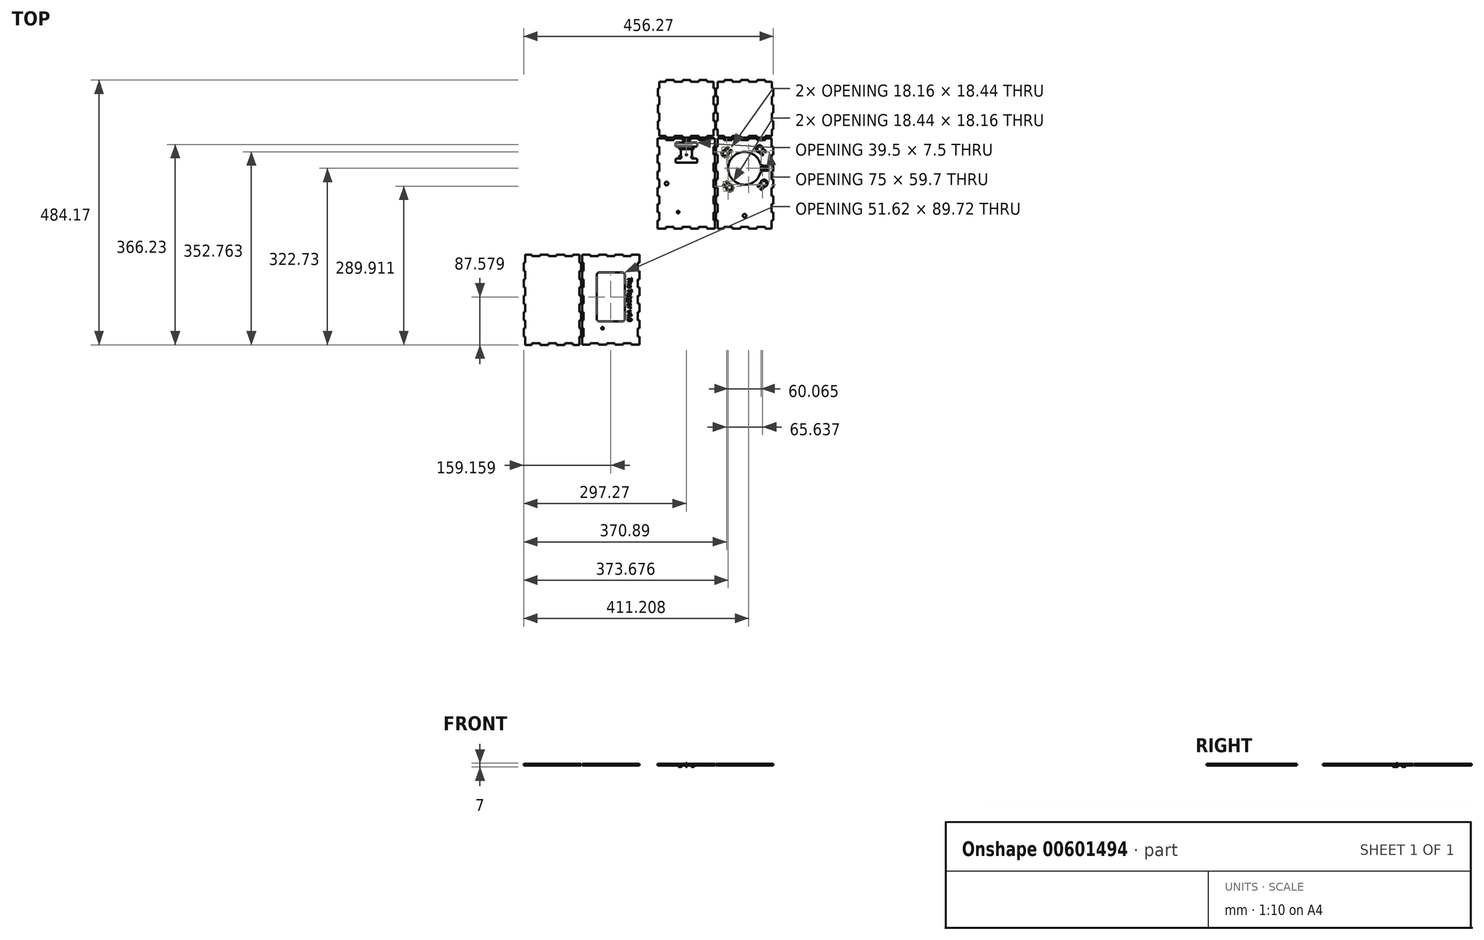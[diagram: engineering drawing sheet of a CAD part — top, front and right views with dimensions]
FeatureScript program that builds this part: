
annotation { "Feature Type Name" : "Feature", "Feature Type Description" : "" }
export const myFeature = defineFeature(function(context is Context, id is Id, definition is map)
    precondition{}
    {
        {
            assignVariable(context, id + "F0", {"name" : "holeNeckDepth", "anyValue" : 3});
        }
        {
            assignVariable(context, id + "F1", {"name" : "woodTh", "anyValue" : 3});
        }
        {
            var Q0;
            Q0=qCreatedBy(makeId("Top.planeOp"),FACE);
            var sketch = newSketch(context, id + "F2", { "sketchPlane" : qUnion([Q0])});
            skLineSegment(sketch, "E0", {"start": v(0, 0) * mm, "end": v(11.88, 0) * mm, "construction": true});
            skLineSegment(sketch, "E1", {"start": v(11.88, 0) * mm, "end": v(11.88, 8.12) * mm, "construction": true});
            skCircle(sketch, "E2", {"center": v(11.88, 8.12) * mm, "radius": 2.88 * mm});
            skCircle(sketch, "E3", {"center": v(11.88, 8.12) * mm, "radius": 1.5 * mm});
            skLineSegment(sketch, "E4", {"start": v(0, 8.12) * mm, "end": v(0, 0) * mm, "construction": true});
            skCircle(sketch, "E5.MirrorC", {"center": v(11.88, -8.12) * mm, "radius": 1.5 * mm});
            skCircle(sketch, "E6.MirrorC", {"center": v(11.88, -8.12) * mm, "radius": 2.88 * mm});
            skCircle(sketch, "E7.MirrorC", {"center": v(-11.88, -8.12) * mm, "radius": 2.88 * mm});
            skCircle(sketch, "E8.MirrorC", {"center": v(-11.88, 8.12) * mm, "radius": 2.88 * mm});
            skCircle(sketch, "E9.MirrorC", {"center": v(-11.88, 8.12) * mm, "radius": 1.5 * mm});
            skCircle(sketch, "E10.MirrorC", {"center": v(-11.88, -8.12) * mm, "radius": 1.5 * mm});
            skLineSegment(sketch, "E11", {"start": v(11.88, -5.25) * mm, "end": v(-11.88, -5.25) * mm, "construction": true});
            skLineSegment(sketch, "E12", {"start": v(0, -5.25) * mm, "end": v(0, -3.75) * mm, "construction": true});
            skPoint(sketch, "E12.endSnap0", {"position": v(0, -5.25) * mm});
            skCircle(sketch, "E13", {"center": v(0, -3.75) * mm, "radius": 1.3 * mm});
            skSolve(sketch);
        }
        {
            var Q0;
            Q0=makeQuery(id+"F2.imprint","IMPRINT",FACE,{"disambiguationData":[TD([[makeQuery(id+"F2.imprint","IMPRINT",EDGE,{"derivedFrom":sQuery(id+"F2.wireOp",EDGE,"E8.MirrorC")}),-1.0]])]});
            var Q1;
            Q1=makeQuery(id+"F2.imprint","IMPRINT",FACE,{"disambiguationData":[TD([[makeQuery(id+"F2.imprint","IMPRINT",EDGE,{"derivedFrom":sQuery(id+"F2.wireOp",EDGE,"E2")}),1.0]])]});
            var Q2;
            Q2=makeQuery(id+"F2.imprint","IMPRINT",FACE,{"disambiguationData":[TD([[makeQuery(id+"F2.imprint","IMPRINT",EDGE,{"derivedFrom":sQuery(id+"F2.wireOp",EDGE,"E5.MirrorC")}),1.0]])]});
            var Q3;
            Q3=makeQuery(id+"F2.imprint","IMPRINT",FACE,{"disambiguationData":[TD([[makeQuery(id+"F2.imprint","IMPRINT",EDGE,{"derivedFrom":sQuery(id+"F2.wireOp",EDGE,"E7.MirrorC")}),1.0]])]});
            extrude(context, id + "F3", {"entities" : qUnion([Q0, Q1, Q2, Q3]), "depth" : (getVariable(context, 'holeNeckDepth') * 2) * mm, "offsetDistance" : 25 * mm});
        }
        {
            var Q0;
            Q0=qCreatedBy(makeId("Top.planeOp"),FACE);
            cPlane(context, id + "F4", {"entities" : qUnion([Q0]), "cplaneType" : CPlaneType.OFFSET, "offset" : (getVariable(context, 'holeNeckDepth') * 2) * mm, "width" : 150 * mm, "height" : 150 * mm});
        }
        {
            var Q0;
            Q0=qCreatedBy(id+"F4.planeOp",FACE);
            var sketch = newSketch(context, id + "F5", { "sketchPlane" : qUnion([Q0])});
            skLineSegment(sketch, "E14", {"start": v(9.42, 6.63) * mm, "end": v(-9.42, 6.63) * mm});
            skLineSegment(sketch, "E15", {"start": v(-11.88, 11) * mm, "end": v(11.88, 11) * mm});
            skLineSegment(sketch, "E16", {"start": v(14.75, 8.12) * mm, "end": v(14.75, -8.12) * mm, "construction": true});
            skLineSegment(sketch, "E17", {"start": v(10.38, 5.67) * mm, "end": v(10.38, -5.67) * mm});
            skLineSegment(sketch, "E18", {"start": v(-10.38, 5.67) * mm, "end": v(-10.38, -5.67) * mm});
            skLineSegment(sketch, "E19", {"start": v(-14.75, 8.12) * mm, "end": v(-14.75, -8.12) * mm, "construction": true});
            skLineSegment(sketch, "E20", {"start": v(11.88, 11) * mm, "end": v(52.5, 11) * mm, "construction": true});
            skArc(sketch, "E21.0", {"start": v(-9.42, 6.63) * mm, "mid": v(-9.84, 6.1) * mm, "end": v(-10.38, 5.67) * mm});
            skArc(sketch, "E22.0", {"start": v(-11.88, -11) * mm, "mid": v(-9.1, -8.9) * mm, "end": v(-10.38, -5.67) * mm});
            skArc(sketch, "E23.0", {"start": v(11.88, -11) * mm, "mid": v(9.1, -8.9) * mm, "end": v(10.38, -5.67) * mm});
            skArc(sketch, "E24.0", {"start": v(9.42, 6.63) * mm, "mid": v(9.84, 6.1) * mm, "end": v(10.38, 5.67) * mm});
            skLineSegment(sketch, "E25.MirrorCS", {"start": v(11.88, -11) * mm, "end": v(52.5, -11) * mm, "construction": true});
            skLineSegment(sketch, "E26.MirrorCS", {"start": v(-11.88, -11) * mm, "end": v(-52.5, -11) * mm, "construction": true});
            skLineSegment(sketch, "E27.MirrorCS", {"start": v(-11.88, 11) * mm, "end": v(-52.5, 11) * mm, "construction": true});
            skCircle(sketch, "E28.0", {"center": v(-11.88, 8.12) * mm, "radius": 1.5 * mm});
            skCircle(sketch, "E29.0", {"center": v(11.88, -8.12) * mm, "radius": 1.5 * mm});
            skCircle(sketch, "E30.0", {"center": v(-11.88, -8.12) * mm, "radius": 1.5 * mm});
            skLineSegment(sketch, "E31", {"start": v(52.5, 26) * mm, "end": v(52.5, 11) * mm});
            skLineSegment(sketch, "E32", {"start": v(52.5, 11) * mm, "end": v(49.5, 11) * mm});
            skLineSegment(sketch, "E33", {"start": v(32.19, 11) * mm, "end": v(32.19, 26) * mm, "construction": true});
            skLineSegment(sketch, "E34", {"start": v(49.5, 11) * mm, "end": v(49.5, -4) * mm});
            skLineSegment(sketch, "E35", {"start": v(49.5, -4) * mm, "end": v(52.5, -4) * mm});
            skLineSegment(sketch, "E36", {"start": v(14.75, 8.12) * mm, "end": v(14.75, 11) * mm, "construction": true});
            skLineSegment(sketch, "E37", {"start": v(14.75, 11) * mm, "end": v(17.75, 11) * mm});
            skLineSegment(sketch, "E38", {"start": v(19.75, 13) * mm, "end": v(19.75, 16.5) * mm});
            skLineSegment(sketch, "E39", {"start": v(17.75, 18.5) * mm, "end": v(0, 18.5) * mm});
            skPoint(sketch, "E39.endSnap0", {"position": v(0, 6.63) * mm});
            skLineSegment(sketch, "E40.MirrorCS", {"start": v(-14.75, 11) * mm, "end": v(-17.75, 11) * mm});
            skLineSegment(sketch, "E41.MirrorCS", {"start": v(-14.75, 8.12) * mm, "end": v(-14.75, 11) * mm, "construction": true});
            skLineSegment(sketch, "E42.MirrorCS", {"start": v(-17.75, 18.5) * mm, "end": v(0, 18.5) * mm});
            skLineSegment(sketch, "E43.MirrorCS", {"start": v(-19.75, 13) * mm, "end": v(-19.75, 16.5) * mm});
            skLineSegment(sketch, "E44.MirrorCS", {"start": v(-14.75, -8.12) * mm, "end": v(-14.75, -11) * mm, "construction": true});
            skLineSegment(sketch, "E45.MirrorCS", {"start": v(14.75, -8.12) * mm, "end": v(14.75, -11) * mm, "construction": true});
            skLineSegment(sketch, "E46.MirrorCS", {"start": v(19.75, -13) * mm, "end": v(19.75, -16.5) * mm});
            skLineSegment(sketch, "E47.MirrorCS", {"start": v(14.75, -11) * mm, "end": v(17.75, -11) * mm});
            skLineSegment(sketch, "E48.MirrorCS", {"start": v(17.75, -18.5) * mm, "end": v(0, -18.5) * mm});
            skLineSegment(sketch, "E49.MirrorCS", {"start": v(-14.75, -11) * mm, "end": v(-17.75, -11) * mm});
            skLineSegment(sketch, "E50.MirrorCS", {"start": v(-19.75, -13) * mm, "end": v(-19.75, -16.5) * mm});
            skLineSegment(sketch, "E51.MirrorCS", {"start": v(-17.75, -18.5) * mm, "end": v(0, -18.5) * mm});
            skLineSegment(sketch, "E52", {"start": v(52.5, 26) * mm, "end": v(45.43, 18.93) * mm, "construction": true});
            skLineSegment(sketch, "E53.MirrorCS", {"start": v(37.5, 26) * mm, "end": v(37.5, 23) * mm});
            skLineSegment(sketch, "E54.MirrorCS", {"start": v(37.5, 23) * mm, "end": v(22.5, 23) * mm});
            skLineSegment(sketch, "E55.MirrorCS", {"start": v(22.5, 23) * mm, "end": v(22.5, 26) * mm});
            skLineSegment(sketch, "E56.MirrorCS", {"start": v(52.5, 26) * mm, "end": v(37.5, 26) * mm});
            skLineSegment(sketch, "E57.1.0.0", {"start": v(7.5, 23) * mm, "end": v(-7.5, 23) * mm});
            skLineSegment(sketch, "E57.1.0.1", {"start": v(-7.5, 23) * mm, "end": v(-7.5, 26) * mm});
            skLineSegment(sketch, "E57.1.0.2", {"start": v(7.5, 26) * mm, "end": v(7.5, 23) * mm});
            skLineSegment(sketch, "E57.1.0.3", {"start": v(22.5, 26) * mm, "end": v(7.5, 26) * mm});
            skLineSegment(sketch, "E57.2.0.0", {"start": v(-22.5, 23) * mm, "end": v(-37.5, 23) * mm});
            skLineSegment(sketch, "E57.2.0.1", {"start": v(-37.5, 23) * mm, "end": v(-37.5, 26) * mm});
            skLineSegment(sketch, "E57.2.0.2", {"start": v(-22.5, 26) * mm, "end": v(-22.5, 23) * mm});
            skLineSegment(sketch, "E57.2.0.3", {"start": v(-7.5, 26) * mm, "end": v(-22.5, 26) * mm});
            skLineSegment(sketch, "E57.direction1", {"start": v(22.5, 23) * mm, "end": v(-7.5, 23) * mm, "construction": true});
            skLineSegment(sketch, "E58", {"start": v(-37.5, 26) * mm, "end": v(-52.5, 26) * mm});
            skLineSegment(sketch, "E59.0.1.0", {"start": v(49.5, -19) * mm, "end": v(49.5, -34) * mm});
            skLineSegment(sketch, "E59.0.1.1", {"start": v(52.5, -4) * mm, "end": v(52.5, -19) * mm});
            skLineSegment(sketch, "E59.0.1.2", {"start": v(49.5, -34) * mm, "end": v(52.5, -34) * mm});
            skLineSegment(sketch, "E59.0.1.3", {"start": v(52.5, -19) * mm, "end": v(49.5, -19) * mm});
            skLineSegment(sketch, "E59.0.2.0", {"start": v(49.5, -49) * mm, "end": v(49.5, -64) * mm});
            skLineSegment(sketch, "E59.0.2.1", {"start": v(52.5, -34) * mm, "end": v(52.5, -49) * mm});
            skLineSegment(sketch, "E59.0.2.2", {"start": v(49.5, -64) * mm, "end": v(52.5, -64) * mm});
            skLineSegment(sketch, "E59.0.2.3", {"start": v(52.5, -49) * mm, "end": v(49.5, -49) * mm});
            skLineSegment(sketch, "E59.0.3.0", {"start": v(49.5, -79) * mm, "end": v(49.5, -94) * mm});
            skLineSegment(sketch, "E59.0.3.1", {"start": v(52.5, -64) * mm, "end": v(52.5, -79) * mm});
            skLineSegment(sketch, "E59.0.3.2", {"start": v(49.5, -94) * mm, "end": v(52.5, -94) * mm});
            skLineSegment(sketch, "E59.0.3.3", {"start": v(52.5, -79) * mm, "end": v(49.5, -79) * mm});
            skLineSegment(sketch, "E59.direction1", {"start": v(49.5, -4) * mm, "end": v(74.5, -4) * mm, "construction": true});
            skLineSegment(sketch, "E59.direction2", {"start": v(49.5, -4) * mm, "end": v(49.5, -34) * mm, "construction": true});
            skLineSegment(sketch, "E60.0.0.4", {"start": v(49.5, -109) * mm, "end": v(49.5, -124) * mm});
            skLineSegment(sketch, "E60.3.0.4", {"start": v(52.5, -94) * mm, "end": v(52.5, -109) * mm});
            skLineSegment(sketch, "E60.6.0.4", {"start": v(49.5, -124) * mm, "end": v(52.5, -124) * mm});
            skLineSegment(sketch, "E60.9.0.4", {"start": v(52.5, -109) * mm, "end": v(49.5, -109) * mm});
            skLineSegment(sketch, "E61", {"start": v(52.5, -124) * mm, "end": v(52.5, -139) * mm});
            skLineSegment(sketch, "E62.MirrorCS", {"start": v(-49.5, -94) * mm, "end": v(-52.5, -94) * mm});
            skLineSegment(sketch, "E63.MirrorCS", {"start": v(-52.5, 11) * mm, "end": v(-49.5, 11) * mm});
            skLineSegment(sketch, "E64.MirrorCS", {"start": v(-49.5, -64) * mm, "end": v(-52.5, -64) * mm});
            skLineSegment(sketch, "E65.MirrorCS", {"start": v(-49.5, -124) * mm, "end": v(-52.5, -124) * mm});
            skLineSegment(sketch, "E66.MirrorCS", {"start": v(-49.5, -4) * mm, "end": v(-52.5, -4) * mm});
            skLineSegment(sketch, "E67.MirrorCS", {"start": v(-52.5, -19) * mm, "end": v(-49.5, -19) * mm});
            skLineSegment(sketch, "E68.MirrorCS", {"start": v(-52.5, -109) * mm, "end": v(-49.5, -109) * mm});
            skLineSegment(sketch, "E69.MirrorCS", {"start": v(-52.5, -79) * mm, "end": v(-49.5, -79) * mm});
            skLineSegment(sketch, "E70.MirrorCS", {"start": v(-52.5, -49) * mm, "end": v(-49.5, -49) * mm});
            skLineSegment(sketch, "E71.MirrorCS", {"start": v(-49.5, -34) * mm, "end": v(-52.5, -34) * mm});
            skLineSegment(sketch, "E72.MirrorCS", {"start": v(-49.5, -19) * mm, "end": v(-49.5, -34) * mm});
            skLineSegment(sketch, "E73.MirrorCS", {"start": v(-49.5, 11) * mm, "end": v(-49.5, -4) * mm});
            skLineSegment(sketch, "E74.MirrorCS", {"start": v(-49.5, -49) * mm, "end": v(-49.5, -64) * mm});
            skLineSegment(sketch, "E75.MirrorCS", {"start": v(-52.5, -4) * mm, "end": v(-52.5, -19) * mm});
            skLineSegment(sketch, "E76.MirrorCS", {"start": v(-49.5, -79) * mm, "end": v(-49.5, -94) * mm});
            skLineSegment(sketch, "E77.MirrorCS", {"start": v(-52.5, 26) * mm, "end": v(-52.5, 11) * mm});
            skLineSegment(sketch, "E78.MirrorCS", {"start": v(-52.5, -34) * mm, "end": v(-52.5, -49) * mm});
            skLineSegment(sketch, "E79.MirrorCS", {"start": v(-49.5, -109) * mm, "end": v(-49.5, -124) * mm});
            skLineSegment(sketch, "E80.MirrorCS", {"start": v(-52.5, -94) * mm, "end": v(-52.5, -109) * mm});
            skLineSegment(sketch, "E81.MirrorCS", {"start": v(-52.5, -124) * mm, "end": v(-52.5, -139) * mm});
            skLineSegment(sketch, "E82.MirrorCS", {"start": v(-52.5, -64) * mm, "end": v(-52.5, -79) * mm});
            skLineSegment(sketch, "E83", {"start": v(49.5, -56.5) * mm, "end": v(-49.5, -56.5) * mm, "construction": true});
            skLineSegment(sketch, "E84.MirrorCS", {"start": v(-37.5, -136) * mm, "end": v(-37.5, -139) * mm});
            skLineSegment(sketch, "E85.MirrorCS", {"start": v(7.5, -139) * mm, "end": v(7.5, -136) * mm});
            skLineSegment(sketch, "E86.MirrorCS", {"start": v(-22.5, -139) * mm, "end": v(-22.5, -136) * mm});
            skLineSegment(sketch, "E87.MirrorCS", {"start": v(22.5, -136) * mm, "end": v(22.5, -139) * mm});
            skLineSegment(sketch, "E88.MirrorCS", {"start": v(-7.5, -136) * mm, "end": v(-7.5, -139) * mm});
            skLineSegment(sketch, "E89.MirrorCS", {"start": v(37.5, -139) * mm, "end": v(37.5, -136) * mm});
            skLineSegment(sketch, "E90.MirrorCS", {"start": v(7.5, -136) * mm, "end": v(-7.5, -136) * mm});
            skLineSegment(sketch, "E91.MirrorCS", {"start": v(-7.5, -139) * mm, "end": v(-22.5, -139) * mm});
            skLineSegment(sketch, "E92.MirrorCS", {"start": v(52.5, -139) * mm, "end": v(37.5, -139) * mm});
            skLineSegment(sketch, "E93.MirrorCS", {"start": v(37.5, -136) * mm, "end": v(22.5, -136) * mm});
            skLineSegment(sketch, "E94.MirrorCS", {"start": v(-22.5, -136) * mm, "end": v(-37.5, -136) * mm});
            skLineSegment(sketch, "E95.MirrorCS", {"start": v(-52.5, -139) * mm, "end": v(-52.5, -124) * mm});
            skLineSegment(sketch, "E96.MirrorCS", {"start": v(-37.5, -139) * mm, "end": v(-52.5, -139) * mm});
            skLineSegment(sketch, "E97.MirrorCS", {"start": v(22.5, -139) * mm, "end": v(7.5, -139) * mm});
            skLineSegment(sketch, "E98.MirrorCS", {"start": v(53.94, -34) * mm, "end": v(56.94, -34) * mm});
            skLineSegment(sketch, "E99.MirrorCS", {"start": v(56.94, 11) * mm, "end": v(53.94, 11) * mm});
            skLineSegment(sketch, "E100.MirrorCS", {"start": v(53.94, -94) * mm, "end": v(56.94, -94) * mm});
            skLineSegment(sketch, "E101.MirrorCS", {"start": v(53.94, -124) * mm, "end": v(56.94, -124) * mm});
            skLineSegment(sketch, "E102.MirrorCS", {"start": v(53.94, -64) * mm, "end": v(56.94, -64) * mm});
            skLineSegment(sketch, "E103.MirrorCS", {"start": v(53.94, -4) * mm, "end": v(56.94, -4) * mm});
            skLineSegment(sketch, "E104.MirrorCS", {"start": v(56.94, -109) * mm, "end": v(53.94, -109) * mm});
            skLineSegment(sketch, "E105.MirrorCS", {"start": v(56.94, -49) * mm, "end": v(53.94, -49) * mm});
            skLineSegment(sketch, "E106.MirrorCS", {"start": v(56.94, -19) * mm, "end": v(53.94, -19) * mm});
            skLineSegment(sketch, "E107.MirrorCS", {"start": v(56.94, -79) * mm, "end": v(53.94, -79) * mm});
            skLineSegment(sketch, "E108.MirrorCS", {"start": v(53.94, -79) * mm, "end": v(53.94, -94) * mm});
            skLineSegment(sketch, "E109.MirrorCS", {"start": v(56.94, -124) * mm, "end": v(56.94, -139) * mm});
            skLineSegment(sketch, "E110.MirrorCS", {"start": v(53.94, -49) * mm, "end": v(53.94, -64) * mm});
            skLineSegment(sketch, "E111.MirrorCS", {"start": v(56.94, -94) * mm, "end": v(56.94, -109) * mm});
            skLineSegment(sketch, "E112.MirrorCS", {"start": v(56.94, -34) * mm, "end": v(56.94, -49) * mm});
            skLineSegment(sketch, "E113.MirrorCS", {"start": v(56.94, 26) * mm, "end": v(56.94, 11) * mm});
            skLineSegment(sketch, "E114.MirrorCS", {"start": v(53.94, -19) * mm, "end": v(53.94, -34) * mm});
            skLineSegment(sketch, "E115.MirrorCS", {"start": v(56.94, -64) * mm, "end": v(56.94, -79) * mm});
            skLineSegment(sketch, "E116.MirrorCS", {"start": v(56.94, -4) * mm, "end": v(56.94, -19) * mm});
            skLineSegment(sketch, "E117.MirrorCS", {"start": v(53.94, -109) * mm, "end": v(53.94, -124) * mm});
            skLineSegment(sketch, "E118.MirrorCS", {"start": v(53.94, 11) * mm, "end": v(53.94, -4) * mm});
            skLineSegment(sketch, "E119", {"start": v(56.94, 26) * mm, "end": v(68.94, 26) * mm});
            skLineSegment(sketch, "E120", {"start": v(68.94, 26) * mm, "end": v(68.94, 23) * mm});
            skLineSegment(sketch, "E121.MirrorCS", {"start": v(69, 132.7) * mm, "end": v(69, 129.7) * mm});
            skLineSegment(sketch, "E122.MirrorCS", {"start": v(114, 129.7) * mm, "end": v(114, 132.7) * mm});
            skLineSegment(sketch, "E123.MirrorCS", {"start": v(84, 129.7) * mm, "end": v(84, 132.7) * mm});
            skLineSegment(sketch, "E124.MirrorCS", {"start": v(129, 132.7) * mm, "end": v(129, 129.7) * mm});
            skLineSegment(sketch, "E125.MirrorCS", {"start": v(99, 132.7) * mm, "end": v(99, 129.7) * mm});
            skLineSegment(sketch, "E126.MirrorCS", {"start": v(144, 129.7) * mm, "end": v(144, 132.7) * mm});
            skLineSegment(sketch, "E127.MirrorCS", {"start": v(114, 132.7) * mm, "end": v(99, 132.7) * mm});
            skLineSegment(sketch, "E128.MirrorCS", {"start": v(99, 129.7) * mm, "end": v(84, 129.7) * mm});
            skLineSegment(sketch, "E129.MirrorCS", {"start": v(144, 132.7) * mm, "end": v(129, 132.7) * mm});
            skLineSegment(sketch, "E130.MirrorCS", {"start": v(84, 132.7) * mm, "end": v(69, 132.7) * mm});
            skLineSegment(sketch, "E131.MirrorCS", {"start": v(129, 129.7) * mm, "end": v(114, 129.7) * mm});
            skLineSegment(sketch, "E132", {"start": v(68.94, 23) * mm, "end": v(83.94, 23) * mm});
            skLineSegment(sketch, "E133", {"start": v(83.94, 23) * mm, "end": v(83.94, 26) * mm});
            skLineSegment(sketch, "E134", {"start": v(83.94, 26) * mm, "end": v(98.94, 26) * mm});
            skLineSegment(sketch, "E135", {"start": v(98.94, 26) * mm, "end": v(98.94, 23) * mm});
            skLineSegment(sketch, "E136", {"start": v(98.94, 23) * mm, "end": v(106.44, 23) * mm});
            skLineSegment(sketch, "E137", {"start": v(106.44, 39.72) * mm, "end": v(106.44, -168.67) * mm, "construction": true});
            skLineSegment(sketch, "E138.MirrorCS", {"start": v(143.94, 23) * mm, "end": v(128.94, 23) * mm});
            skLineSegment(sketch, "E139.MirrorCS", {"start": v(113.94, 23) * mm, "end": v(106.44, 23) * mm});
            skLineSegment(sketch, "E140.MirrorCS", {"start": v(128.94, 23) * mm, "end": v(128.94, 26) * mm});
            skLineSegment(sketch, "E141.MirrorCS", {"start": v(155.94, 26) * mm, "end": v(143.94, 26) * mm});
            skLineSegment(sketch, "E142.MirrorCS", {"start": v(128.94, 26) * mm, "end": v(113.94, 26) * mm});
            skLineSegment(sketch, "E143.MirrorCS", {"start": v(113.94, 26) * mm, "end": v(113.94, 23) * mm});
            skLineSegment(sketch, "E144.MirrorCS", {"start": v(143.94, 26) * mm, "end": v(143.94, 23) * mm});
            skLineSegment(sketch, "E145", {"start": v(53.94, -56.5) * mm, "end": v(167.2, -56.5) * mm, "construction": true});
            skLineSegment(sketch, "E146.MirrorCS", {"start": v(155.94, -79) * mm, "end": v(158.94, -79) * mm});
            skLineSegment(sketch, "E147.MirrorCS", {"start": v(158.94, -4) * mm, "end": v(155.94, -4) * mm});
            skLineSegment(sketch, "E148.MirrorCS", {"start": v(155.94, -49) * mm, "end": v(158.94, -49) * mm});
            skLineSegment(sketch, "E149.MirrorCS", {"start": v(155.94, -109) * mm, "end": v(158.94, -109) * mm});
            skLineSegment(sketch, "E150.MirrorCS", {"start": v(158.94, -94) * mm, "end": v(155.94, -94) * mm});
            skLineSegment(sketch, "E151.MirrorCS", {"start": v(158.94, -124) * mm, "end": v(155.94, -124) * mm});
            skLineSegment(sketch, "E152.MirrorCS", {"start": v(158.94, -64) * mm, "end": v(155.94, -64) * mm});
            skLineSegment(sketch, "E153.MirrorCS", {"start": v(155.94, 11) * mm, "end": v(158.94, 11) * mm});
            skLineSegment(sketch, "E154.MirrorCS", {"start": v(155.94, -19) * mm, "end": v(158.94, -19) * mm});
            skLineSegment(sketch, "E155.MirrorCS", {"start": v(158.94, -34) * mm, "end": v(155.94, -34) * mm});
            skLineSegment(sketch, "E156.MirrorCS", {"start": v(158.94, 11) * mm, "end": v(158.94, -4) * mm});
            skLineSegment(sketch, "E157.MirrorCS", {"start": v(158.94, -109) * mm, "end": v(158.94, -124) * mm});
            skLineSegment(sketch, "E158.MirrorCS", {"start": v(155.94, -64) * mm, "end": v(155.94, -79) * mm});
            skLineSegment(sketch, "E159.MirrorCS", {"start": v(155.94, -4) * mm, "end": v(155.94, -19) * mm});
            skLineSegment(sketch, "E160.MirrorCS", {"start": v(155.94, -34) * mm, "end": v(155.94, -49) * mm});
            skLineSegment(sketch, "E161.MirrorCS", {"start": v(155.94, -94) * mm, "end": v(155.94, -109) * mm});
            skLineSegment(sketch, "E162.MirrorCS", {"start": v(158.94, -49) * mm, "end": v(158.94, -64) * mm});
            skLineSegment(sketch, "E163.MirrorCS", {"start": v(158.94, -79) * mm, "end": v(158.94, -94) * mm});
            skLineSegment(sketch, "E164.MirrorCS", {"start": v(155.94, -124) * mm, "end": v(155.94, -139) * mm});
            skLineSegment(sketch, "E165.MirrorCS", {"start": v(158.94, -19) * mm, "end": v(158.94, -34) * mm});
            skLineSegment(sketch, "E166.MirrorCS", {"start": v(155.94, 26) * mm, "end": v(155.94, 11) * mm});
            skLineSegment(sketch, "E167.MirrorCS", {"start": v(83.94, -136) * mm, "end": v(83.94, -139) * mm});
            skLineSegment(sketch, "E168.MirrorCS", {"start": v(113.94, -139) * mm, "end": v(113.94, -136) * mm});
            skLineSegment(sketch, "E169.MirrorCS", {"start": v(98.94, -139) * mm, "end": v(98.94, -136) * mm});
            skLineSegment(sketch, "E170.MirrorCS", {"start": v(68.94, -139) * mm, "end": v(68.94, -136) * mm});
            skLineSegment(sketch, "E171.MirrorCS", {"start": v(128.94, -136) * mm, "end": v(128.94, -139) * mm});
            skLineSegment(sketch, "E172.MirrorCS", {"start": v(143.94, -139) * mm, "end": v(143.94, -136) * mm});
            skLineSegment(sketch, "E173.MirrorCS", {"start": v(56.94, -139) * mm, "end": v(68.94, -139) * mm});
            skLineSegment(sketch, "E174.MirrorCS", {"start": v(98.94, -136) * mm, "end": v(106.44, -136) * mm});
            skLineSegment(sketch, "E175.MirrorCS", {"start": v(68.94, -136) * mm, "end": v(83.94, -136) * mm});
            skLineSegment(sketch, "E176.MirrorCS", {"start": v(83.94, -139) * mm, "end": v(98.94, -139) * mm});
            skLineSegment(sketch, "E177.MirrorCS", {"start": v(143.94, -136) * mm, "end": v(128.94, -136) * mm});
            skLineSegment(sketch, "E178.MirrorCS", {"start": v(113.94, -136) * mm, "end": v(106.44, -136) * mm});
            skLineSegment(sketch, "E179.MirrorCS", {"start": v(155.94, -139) * mm, "end": v(143.94, -139) * mm});
            skLineSegment(sketch, "E180.MirrorCS", {"start": v(128.94, -139) * mm, "end": v(113.94, -139) * mm});
            skLineSegment(sketch, "E181", {"start": v(144, 129.7) * mm, "end": v(156, 129.7) * mm});
            skLineSegment(sketch, "E182.MirrorCS", {"start": v(159, 102.7) * mm, "end": v(156, 102.7) * mm});
            skLineSegment(sketch, "E183.MirrorCS", {"start": v(156, 72.7) * mm, "end": v(159, 72.7) * mm});
            skLineSegment(sketch, "E184.MirrorCS", {"start": v(156, 87.7) * mm, "end": v(159, 87.7) * mm});
            skLineSegment(sketch, "E185.MirrorCS", {"start": v(156, 117.7) * mm, "end": v(159, 117.7) * mm});
            skLineSegment(sketch, "E186.MirrorCS", {"start": v(159, 57.7) * mm, "end": v(156, 57.7) * mm});
            skLineSegment(sketch, "E187.MirrorCS", {"start": v(156, 42.7) * mm, "end": v(159, 42.7) * mm});
            skLineSegment(sketch, "E188.MirrorCS", {"start": v(156, 129.7) * mm, "end": v(156, 117.7) * mm});
            skLineSegment(sketch, "E189.MirrorCS", {"start": v(159, 87.7) * mm, "end": v(159, 80.2) * mm});
            skLineSegment(sketch, "E190.MirrorCS", {"start": v(159, 117.7) * mm, "end": v(159, 102.7) * mm});
            skLineSegment(sketch, "E191.MirrorCS", {"start": v(156, 102.7) * mm, "end": v(156, 87.7) * mm});
            skLineSegment(sketch, "E192.MirrorCS", {"start": v(159, 42.7) * mm, "end": v(159, 57.7) * mm});
            skLineSegment(sketch, "E193.MirrorCS", {"start": v(159, 72.7) * mm, "end": v(159, 80.2) * mm});
            skLineSegment(sketch, "E194.MirrorCS", {"start": v(156, 30.7) * mm, "end": v(156, 42.7) * mm});
            skLineSegment(sketch, "E195.MirrorCS", {"start": v(156, 57.7) * mm, "end": v(156, 72.7) * mm});
            skLineSegment(sketch, "E196", {"start": v(106.5, 132.7) * mm, "end": v(106.5, 56.18) * mm, "construction": true});
            skPoint(sketch, "E196.endSnap0", {"position": v(106.5, 132.7) * mm});
            skLineSegment(sketch, "E197.MirrorCS", {"start": v(69, 129.7) * mm, "end": v(57, 129.7) * mm});
            skLineSegment(sketch, "E198.MirrorCS", {"start": v(54, 102.7) * mm, "end": v(57, 102.7) * mm});
            skLineSegment(sketch, "E199.MirrorCS", {"start": v(54, 57.7) * mm, "end": v(57, 57.7) * mm});
            skLineSegment(sketch, "E200.MirrorCS", {"start": v(57, 117.7) * mm, "end": v(54, 117.7) * mm});
            skLineSegment(sketch, "E201.MirrorCS", {"start": v(57, 42.7) * mm, "end": v(54, 42.7) * mm});
            skLineSegment(sketch, "E202.MirrorCS", {"start": v(57, 87.7) * mm, "end": v(54, 87.7) * mm});
            skLineSegment(sketch, "E203.MirrorCS", {"start": v(57, 72.7) * mm, "end": v(54, 72.7) * mm});
            skLineSegment(sketch, "E204.MirrorCS", {"start": v(57, 102.7) * mm, "end": v(57, 87.7) * mm});
            skLineSegment(sketch, "E205.MirrorCS", {"start": v(57, 30.7) * mm, "end": v(57, 42.7) * mm});
            skLineSegment(sketch, "E206.MirrorCS", {"start": v(57, 57.7) * mm, "end": v(57, 72.7) * mm});
            skLineSegment(sketch, "E207.MirrorCS", {"start": v(54, 87.7) * mm, "end": v(54, 80.2) * mm});
            skLineSegment(sketch, "E208.MirrorCS", {"start": v(54, 42.7) * mm, "end": v(54, 57.7) * mm});
            skLineSegment(sketch, "E209.MirrorCS", {"start": v(54, 72.7) * mm, "end": v(54, 80.2) * mm});
            skLineSegment(sketch, "E210.MirrorCS", {"start": v(54, 117.7) * mm, "end": v(54, 102.7) * mm});
            skLineSegment(sketch, "E211.MirrorCS", {"start": v(57, 129.7) * mm, "end": v(57, 117.7) * mm});
            skLineSegment(sketch, "E212", {"start": v(159, 80.2) * mm, "end": v(54, 80.2) * mm, "construction": true});
            skLineSegment(sketch, "E213.MirrorCS", {"start": v(144, 30.7) * mm, "end": v(156, 30.7) * mm});
            skLineSegment(sketch, "E214.MirrorCS", {"start": v(69, 30.7) * mm, "end": v(57, 30.7) * mm});
            skLineSegment(sketch, "E215.MirrorCS", {"start": v(114, 30.7) * mm, "end": v(114, 27.7) * mm});
            skLineSegment(sketch, "E216.MirrorCS", {"start": v(69, 27.7) * mm, "end": v(69, 30.7) * mm});
            skLineSegment(sketch, "E217.MirrorCS", {"start": v(84, 30.7) * mm, "end": v(84, 27.7) * mm});
            skLineSegment(sketch, "E218.MirrorCS", {"start": v(99, 27.7) * mm, "end": v(99, 30.7) * mm});
            skLineSegment(sketch, "E219.MirrorCS", {"start": v(144, 30.7) * mm, "end": v(144, 27.7) * mm});
            skLineSegment(sketch, "E220.MirrorCS", {"start": v(129, 27.7) * mm, "end": v(129, 30.7) * mm});
            skLineSegment(sketch, "E221.MirrorCS", {"start": v(129, 30.7) * mm, "end": v(114, 30.7) * mm});
            skPoint(sketch, "E222.MirrorP", {"position": v(106.5, 27.7) * mm});
            skLineSegment(sketch, "E223.MirrorCS", {"start": v(144, 27.7) * mm, "end": v(129, 27.7) * mm});
            skLineSegment(sketch, "E224.MirrorCS", {"start": v(99, 30.7) * mm, "end": v(84, 30.7) * mm});
            skLineSegment(sketch, "E225.MirrorCS", {"start": v(114, 27.7) * mm, "end": v(99, 27.7) * mm});
            skLineSegment(sketch, "E226.MirrorCS", {"start": v(84, 27.7) * mm, "end": v(69, 27.7) * mm});
            skLineSegment(sketch, "E227", {"start": v(-11.88, 11) * mm, "end": v(-14.75, 11) * mm});
            skLineSegment(sketch, "E228", {"start": v(14.75, 11) * mm, "end": v(11.88, 11) * mm});
            skLineSegment(sketch, "E229", {"start": v(14.75, -11) * mm, "end": v(11.88, -11) * mm});
            skLineSegment(sketch, "E230", {"start": v(-11.88, -11) * mm, "end": v(-14.75, -11) * mm});
            skPoint(sketch, "E231.visualSharp", {"position": v(19.75, 11) * mm});
            skArc(sketch, "E231.filletArc", {"start": v(17.75, 11) * mm, "mid": v(19.16, 11.59) * mm, "end": v(19.75, 13) * mm});
            skPoint(sketch, "E232.visualSharp", {"position": v(19.75, 18.5) * mm});
            skArc(sketch, "E232.filletArc", {"start": v(19.75, 16.5) * mm, "mid": v(19.16, 17.91) * mm, "end": v(17.75, 18.5) * mm});
            skPoint(sketch, "E233.visualSharp", {"position": v(-19.75, 18.5) * mm});
            skArc(sketch, "E233.filletArc", {"start": v(-17.75, 18.5) * mm, "mid": v(-19.16, 17.91) * mm, "end": v(-19.75, 16.5) * mm});
            skPoint(sketch, "E234.visualSharp", {"position": v(-19.75, 11) * mm});
            skArc(sketch, "E234.filletArc", {"start": v(-19.75, 13) * mm, "mid": v(-19.16, 11.59) * mm, "end": v(-17.75, 11) * mm});
            skPoint(sketch, "E235.visualSharp", {"position": v(-19.75, -11) * mm});
            skArc(sketch, "E235.filletArc", {"start": v(-17.75, -11) * mm, "mid": v(-19.16, -11.59) * mm, "end": v(-19.75, -13) * mm});
            skPoint(sketch, "E236.visualSharp", {"position": v(-19.75, -18.5) * mm});
            skArc(sketch, "E236.filletArc", {"start": v(-19.75, -16.5) * mm, "mid": v(-19.16, -17.91) * mm, "end": v(-17.75, -18.5) * mm});
            skPoint(sketch, "E237.visualSharp", {"position": v(19.75, -18.5) * mm});
            skArc(sketch, "E237.filletArc", {"start": v(17.75, -18.5) * mm, "mid": v(19.16, -17.91) * mm, "end": v(19.75, -16.5) * mm});
            skPoint(sketch, "E238.visualSharp", {"position": v(19.75, -11) * mm});
            skArc(sketch, "E238.filletArc", {"start": v(19.75, -13) * mm, "mid": v(19.16, -11.59) * mm, "end": v(17.75, -11) * mm});
            skCircle(sketch, "E239.MirrorC", {"center": v(11.88, 8.12) * mm, "radius": 1.5 * mm});
            skCircle(sketch, "E240.0", {"center": v(0, -3.75) * mm, "radius": 1.3 * mm, "construction": true});
            skLineSegment(sketch, "E241", {"start": v(0, -3.75) * mm, "end": v(0, -28.75) * mm, "construction": true});
            skArc(sketch, "E242", {"start": v(136.17, -32.74) * mm, "mid": v(136.44, -28.75) * mm, "end": v(136.17, -24.76) * mm});
            skLineSegment(sketch, "E243", {"start": v(85.68, -50.4) * mm, "end": v(106.44, -28.75) * mm, "construction": true});
            skLineSegment(sketch, "E244", {"start": v(106.44, -28.75) * mm, "end": v(127.2, -7.1) * mm, "construction": true});
            skLineSegment(sketch, "E245", {"start": v(106.44, -28.75) * mm, "end": v(128.1, -49.5) * mm, "construction": true});
            skLineSegment(sketch, "E246", {"start": v(106.44, -28.75) * mm, "end": v(84.78, -8) * mm, "construction": true});
            skLineSegment(sketch, "E247", {"start": v(85.68, -50.4) * mm, "end": v(77.37, -59.07) * mm, "construction": true});
            skLineSegment(sketch, "E248", {"start": v(77.37, -59.07) * mm, "end": v(78.73, -60.37) * mm});
            skLineSegment(sketch, "E249", {"start": v(77.37, -59.07) * mm, "end": v(72.68, -54.57) * mm});
            skLineSegment(sketch, "E250.0", {"start": v(73.91, -62.68) * mm, "end": v(75.27, -63.98) * mm});
            skLineSegment(sketch, "E250.1", {"start": v(73.91, -62.68) * mm, "end": v(69.22, -58.18) * mm});
            skLineSegment(sketch, "E251", {"start": v(80.98, -62.53) * mm, "end": v(77.52, -66.14) * mm, "construction": true});
            skArc(sketch, "E252", {"start": v(75.27, -63.98) * mm, "mid": v(82.14, -67.1) * mm, "end": v(78.73, -60.37) * mm});
            skLineSegment(sketch, "E253.0", {"start": v(72.18, -64.48) * mm, "end": v(67.5, -59.99) * mm});
            skLineSegment(sketch, "E253.1", {"start": v(79.1, -57.27) * mm, "end": v(74.41, -52.77) * mm});
            skLineSegment(sketch, "E253.2", {"start": v(79.1, -57.27) * mm, "end": v(79.72, -57.85) * mm});
            skArc(sketch, "E253.3", {"start": v(72.8, -65.07) * mm, "mid": v(83.95, -68.83) * mm, "end": v(79.72, -57.85) * mm});
            skLineSegment(sketch, "E253.4", {"start": v(72.18, -64.48) * mm, "end": v(72.8, -65.07) * mm});
            skLineSegment(sketch, "E254", {"start": v(67.8, -58.21) * mm, "end": v(67.46, -58.57) * mm});
            skLineSegment(sketch, "E255", {"start": v(72.65, -53.16) * mm, "end": v(73, -52.8) * mm});
            skLineSegment(sketch, "E256.MirrorCS", {"start": v(-297.27, -246.48) * mm, "end": v(-294.27, -246.48) * mm});
            skLineSegment(sketch, "E257.MirrorCS", {"start": v(-294.27, -201.48) * mm, "end": v(-297.27, -201.48) * mm});
            skLineSegment(sketch, "E258.MirrorCS", {"start": v(-297.27, -306.48) * mm, "end": v(-294.27, -306.48) * mm});
            skLineSegment(sketch, "E259.MirrorCS", {"start": v(-297.27, -336.48) * mm, "end": v(-294.27, -336.48) * mm});
            skLineSegment(sketch, "E260.MirrorCS", {"start": v(-297.27, -276.48) * mm, "end": v(-294.27, -276.48) * mm});
            skLineSegment(sketch, "E261.MirrorCS", {"start": v(-297.27, -216.48) * mm, "end": v(-294.27, -216.48) * mm});
            skLineSegment(sketch, "E262.MirrorCS", {"start": v(-294.27, -321.48) * mm, "end": v(-297.27, -321.48) * mm});
            skLineSegment(sketch, "E263.MirrorCS", {"start": v(-294.27, -261.48) * mm, "end": v(-297.27, -261.48) * mm});
            skLineSegment(sketch, "E264.MirrorCS", {"start": v(-294.27, -231.48) * mm, "end": v(-297.27, -231.48) * mm});
            skLineSegment(sketch, "E265.MirrorCS", {"start": v(-294.27, -291.48) * mm, "end": v(-297.27, -291.48) * mm});
            skLineSegment(sketch, "E266.MirrorCS", {"start": v(-297.27, -291.48) * mm, "end": v(-297.27, -306.48) * mm});
            skLineSegment(sketch, "E267.MirrorCS", {"start": v(-294.27, -336.48) * mm, "end": v(-294.27, -351.48) * mm});
            skLineSegment(sketch, "E268.MirrorCS", {"start": v(-297.27, -261.48) * mm, "end": v(-297.27, -276.48) * mm});
            skLineSegment(sketch, "E269.MirrorCS", {"start": v(-294.27, -306.48) * mm, "end": v(-294.27, -321.48) * mm});
            skLineSegment(sketch, "E270.MirrorCS", {"start": v(-294.27, -246.48) * mm, "end": v(-294.27, -261.48) * mm});
            skLineSegment(sketch, "E271.MirrorCS", {"start": v(-294.27, -186.48) * mm, "end": v(-294.27, -201.48) * mm});
            skLineSegment(sketch, "E272.MirrorCS", {"start": v(-297.27, -231.48) * mm, "end": v(-297.27, -246.48) * mm});
            skLineSegment(sketch, "E273.MirrorCS", {"start": v(-294.27, -276.48) * mm, "end": v(-294.27, -291.48) * mm});
            skLineSegment(sketch, "E274.MirrorCS", {"start": v(-294.27, -216.48) * mm, "end": v(-294.27, -231.48) * mm});
            skLineSegment(sketch, "E275.MirrorCS", {"start": v(-297.27, -321.48) * mm, "end": v(-297.27, -336.48) * mm});
            skLineSegment(sketch, "E276.MirrorCS", {"start": v(-297.27, -201.48) * mm, "end": v(-297.27, -216.48) * mm});
            skLineSegment(sketch, "E277", {"start": v(-294.27, -186.48) * mm, "end": v(-282.27, -186.48) * mm});
            skLineSegment(sketch, "E278", {"start": v(-282.27, -186.48) * mm, "end": v(-282.27, -189.48) * mm});
            skLineSegment(sketch, "E279", {"start": v(-282.27, -189.48) * mm, "end": v(-267.27, -189.48) * mm});
            skLineSegment(sketch, "E280", {"start": v(-267.27, -189.48) * mm, "end": v(-267.27, -186.48) * mm});
            skLineSegment(sketch, "E281", {"start": v(-267.27, -186.48) * mm, "end": v(-252.27, -186.48) * mm});
            skLineSegment(sketch, "E282", {"start": v(-252.27, -186.48) * mm, "end": v(-252.27, -189.48) * mm});
            skLineSegment(sketch, "E283", {"start": v(-252.27, -189.48) * mm, "end": v(-244.77, -189.48) * mm});
            skLineSegment(sketch, "E284", {"start": v(-244.77, -172.76) * mm, "end": v(-244.77, -381.15) * mm, "construction": true});
            skLineSegment(sketch, "E285.MirrorCS", {"start": v(-207.27, -189.48) * mm, "end": v(-222.27, -189.48) * mm});
            skLineSegment(sketch, "E286.MirrorCS", {"start": v(-237.27, -189.48) * mm, "end": v(-244.77, -189.48) * mm});
            skLineSegment(sketch, "E287.MirrorCS", {"start": v(-222.27, -189.48) * mm, "end": v(-222.27, -186.48) * mm});
            skLineSegment(sketch, "E288.MirrorCS", {"start": v(-195.27, -186.48) * mm, "end": v(-207.27, -186.48) * mm});
            skLineSegment(sketch, "E289.MirrorCS", {"start": v(-222.27, -186.48) * mm, "end": v(-237.27, -186.48) * mm});
            skLineSegment(sketch, "E290.MirrorCS", {"start": v(-237.27, -186.48) * mm, "end": v(-237.27, -189.48) * mm});
            skLineSegment(sketch, "E291.MirrorCS", {"start": v(-207.27, -186.48) * mm, "end": v(-207.27, -189.48) * mm});
            skLineSegment(sketch, "E292", {"start": v(-297.27, -268.98) * mm, "end": v(-184.02, -268.98) * mm, "construction": true});
            skLineSegment(sketch, "E293.MirrorCS", {"start": v(-195.27, -291.48) * mm, "end": v(-192.27, -291.48) * mm});
            skLineSegment(sketch, "E294.MirrorCS", {"start": v(-192.27, -216.48) * mm, "end": v(-195.27, -216.48) * mm});
            skLineSegment(sketch, "E295.MirrorCS", {"start": v(-195.27, -261.48) * mm, "end": v(-192.27, -261.48) * mm});
            skLineSegment(sketch, "E296.MirrorCS", {"start": v(-195.27, -321.48) * mm, "end": v(-192.27, -321.48) * mm});
            skLineSegment(sketch, "E297.MirrorCS", {"start": v(-192.27, -306.48) * mm, "end": v(-195.27, -306.48) * mm});
            skLineSegment(sketch, "E298.MirrorCS", {"start": v(-192.27, -336.48) * mm, "end": v(-195.27, -336.48) * mm});
            skLineSegment(sketch, "E299.MirrorCS", {"start": v(-192.27, -276.48) * mm, "end": v(-195.27, -276.48) * mm});
            skLineSegment(sketch, "E300.MirrorCS", {"start": v(-195.27, -201.48) * mm, "end": v(-192.27, -201.48) * mm});
            skLineSegment(sketch, "E301.MirrorCS", {"start": v(-195.27, -231.48) * mm, "end": v(-192.27, -231.48) * mm});
            skLineSegment(sketch, "E302.MirrorCS", {"start": v(-192.27, -246.48) * mm, "end": v(-195.27, -246.48) * mm});
            skLineSegment(sketch, "E303.MirrorCS", {"start": v(-192.27, -201.48) * mm, "end": v(-192.27, -216.48) * mm});
            skLineSegment(sketch, "E304.MirrorCS", {"start": v(-192.27, -321.48) * mm, "end": v(-192.27, -336.48) * mm});
            skLineSegment(sketch, "E305.MirrorCS", {"start": v(-195.27, -276.48) * mm, "end": v(-195.27, -291.48) * mm});
            skLineSegment(sketch, "E306.MirrorCS", {"start": v(-195.27, -216.48) * mm, "end": v(-195.27, -231.48) * mm});
            skLineSegment(sketch, "E307.MirrorCS", {"start": v(-195.27, -246.48) * mm, "end": v(-195.27, -261.48) * mm});
            skLineSegment(sketch, "E308.MirrorCS", {"start": v(-195.27, -306.48) * mm, "end": v(-195.27, -321.48) * mm});
            skLineSegment(sketch, "E309.MirrorCS", {"start": v(-192.27, -261.48) * mm, "end": v(-192.27, -276.48) * mm});
            skLineSegment(sketch, "E310.MirrorCS", {"start": v(-192.27, -291.48) * mm, "end": v(-192.27, -306.48) * mm});
            skLineSegment(sketch, "E311.MirrorCS", {"start": v(-195.27, -336.48) * mm, "end": v(-195.27, -351.48) * mm});
            skLineSegment(sketch, "E312.MirrorCS", {"start": v(-192.27, -231.48) * mm, "end": v(-192.27, -246.48) * mm});
            skLineSegment(sketch, "E313.MirrorCS", {"start": v(-195.27, -186.48) * mm, "end": v(-195.27, -201.48) * mm});
            skLineSegment(sketch, "E314.MirrorCS", {"start": v(-267.27, -348.48) * mm, "end": v(-267.27, -351.48) * mm});
            skLineSegment(sketch, "E315.MirrorCS", {"start": v(-237.27, -351.48) * mm, "end": v(-237.27, -348.48) * mm});
            skLineSegment(sketch, "E316.MirrorCS", {"start": v(-252.27, -351.48) * mm, "end": v(-252.27, -348.48) * mm});
            skLineSegment(sketch, "E317.MirrorCS", {"start": v(-282.27, -351.48) * mm, "end": v(-282.27, -348.48) * mm});
            skLineSegment(sketch, "E318.MirrorCS", {"start": v(-222.27, -348.48) * mm, "end": v(-222.27, -351.48) * mm});
            skLineSegment(sketch, "E319.MirrorCS", {"start": v(-207.27, -351.48) * mm, "end": v(-207.27, -348.48) * mm});
            skLineSegment(sketch, "E320.MirrorCS", {"start": v(-294.27, -351.48) * mm, "end": v(-282.27, -351.48) * mm});
            skLineSegment(sketch, "E321.MirrorCS", {"start": v(-252.27, -348.48) * mm, "end": v(-244.77, -348.48) * mm});
            skLineSegment(sketch, "E322.MirrorCS", {"start": v(-282.27, -348.48) * mm, "end": v(-267.27, -348.48) * mm});
            skLineSegment(sketch, "E323.MirrorCS", {"start": v(-267.27, -351.48) * mm, "end": v(-252.27, -351.48) * mm});
            skLineSegment(sketch, "E324.MirrorCS", {"start": v(-207.27, -348.48) * mm, "end": v(-222.27, -348.48) * mm});
            skLineSegment(sketch, "E325.MirrorCS", {"start": v(-237.27, -348.48) * mm, "end": v(-244.77, -348.48) * mm});
            skLineSegment(sketch, "E326.MirrorCS", {"start": v(-195.27, -351.48) * mm, "end": v(-207.27, -351.48) * mm});
            skLineSegment(sketch, "E327.MirrorCS", {"start": v(-222.27, -351.48) * mm, "end": v(-237.27, -351.48) * mm});
            skLineSegment(sketch, "E328.MirrorCS", {"start": v(-37.17, 132.63) * mm, "end": v(-37.17, 129.63) * mm});
            skLineSegment(sketch, "E329.MirrorCS", {"start": v(7.83, 129.63) * mm, "end": v(7.83, 132.63) * mm});
            skLineSegment(sketch, "E330.MirrorCS", {"start": v(-22.17, 129.63) * mm, "end": v(-22.17, 132.63) * mm});
            skLineSegment(sketch, "E331.MirrorCS", {"start": v(22.83, 132.63) * mm, "end": v(22.83, 129.63) * mm});
            skLineSegment(sketch, "E332.MirrorCS", {"start": v(-7.17, 132.63) * mm, "end": v(-7.17, 129.63) * mm});
            skLineSegment(sketch, "E333.MirrorCS", {"start": v(37.83, 129.63) * mm, "end": v(37.83, 132.63) * mm});
            skLineSegment(sketch, "E334.MirrorCS", {"start": v(7.83, 132.63) * mm, "end": v(-7.17, 132.63) * mm});
            skLineSegment(sketch, "E335.MirrorCS", {"start": v(-7.17, 129.63) * mm, "end": v(-22.17, 129.63) * mm});
            skLineSegment(sketch, "E336.MirrorCS", {"start": v(37.83, 132.63) * mm, "end": v(22.83, 132.63) * mm});
            skLineSegment(sketch, "E337.MirrorCS", {"start": v(-22.17, 132.63) * mm, "end": v(-37.17, 132.63) * mm});
            skLineSegment(sketch, "E338.MirrorCS", {"start": v(22.83, 129.63) * mm, "end": v(7.83, 129.63) * mm});
            skLineSegment(sketch, "E339", {"start": v(37.83, 129.63) * mm, "end": v(49.83, 129.63) * mm});
            skLineSegment(sketch, "E340.MirrorCS", {"start": v(52.83, 102.63) * mm, "end": v(49.83, 102.63) * mm});
            skLineSegment(sketch, "E341.MirrorCS", {"start": v(49.83, 72.63) * mm, "end": v(52.83, 72.63) * mm});
            skLineSegment(sketch, "E342.MirrorCS", {"start": v(49.83, 87.63) * mm, "end": v(52.83, 87.63) * mm});
            skLineSegment(sketch, "E343.MirrorCS", {"start": v(49.83, 117.63) * mm, "end": v(52.83, 117.63) * mm});
            skLineSegment(sketch, "E344.MirrorCS", {"start": v(52.83, 57.63) * mm, "end": v(49.83, 57.63) * mm});
            skLineSegment(sketch, "E345.MirrorCS", {"start": v(49.83, 42.63) * mm, "end": v(52.83, 42.63) * mm});
            skLineSegment(sketch, "E346.MirrorCS", {"start": v(49.83, 129.63) * mm, "end": v(49.83, 117.63) * mm});
            skLineSegment(sketch, "E347.MirrorCS", {"start": v(52.83, 87.63) * mm, "end": v(52.83, 80.13) * mm});
            skLineSegment(sketch, "E348.MirrorCS", {"start": v(52.83, 117.63) * mm, "end": v(52.83, 102.63) * mm});
            skLineSegment(sketch, "E349.MirrorCS", {"start": v(49.83, 102.63) * mm, "end": v(49.83, 87.63) * mm});
            skLineSegment(sketch, "E350.MirrorCS", {"start": v(52.83, 42.63) * mm, "end": v(52.83, 57.63) * mm});
            skLineSegment(sketch, "E351.MirrorCS", {"start": v(52.83, 72.63) * mm, "end": v(52.83, 80.13) * mm});
            skLineSegment(sketch, "E352.MirrorCS", {"start": v(49.83, 30.63) * mm, "end": v(49.83, 42.63) * mm});
            skLineSegment(sketch, "E353.MirrorCS", {"start": v(49.83, 57.63) * mm, "end": v(49.83, 72.63) * mm});
            skLineSegment(sketch, "E354", {"start": v(0.33, 132.63) * mm, "end": v(0.33, 56.1) * mm, "construction": true});
            skPoint(sketch, "E354.endSnap0", {"position": v(0.33, 132.63) * mm});
            skLineSegment(sketch, "E355.MirrorCS", {"start": v(-37.17, 129.63) * mm, "end": v(-49.17, 129.63) * mm});
            skLineSegment(sketch, "E356.MirrorCS", {"start": v(-52.17, 102.63) * mm, "end": v(-49.17, 102.63) * mm});
            skLineSegment(sketch, "E357.MirrorCS", {"start": v(-52.17, 57.63) * mm, "end": v(-49.17, 57.63) * mm});
            skLineSegment(sketch, "E358.MirrorCS", {"start": v(-49.17, 117.63) * mm, "end": v(-52.17, 117.63) * mm});
            skLineSegment(sketch, "E359.MirrorCS", {"start": v(-49.17, 42.63) * mm, "end": v(-52.17, 42.63) * mm});
            skLineSegment(sketch, "E360.MirrorCS", {"start": v(-49.17, 87.63) * mm, "end": v(-52.17, 87.63) * mm});
            skLineSegment(sketch, "E361.MirrorCS", {"start": v(-49.17, 72.63) * mm, "end": v(-52.17, 72.63) * mm});
            skLineSegment(sketch, "E362.MirrorCS", {"start": v(-49.17, 102.63) * mm, "end": v(-49.17, 87.63) * mm});
            skLineSegment(sketch, "E363.MirrorCS", {"start": v(-49.17, 30.63) * mm, "end": v(-49.17, 42.63) * mm});
            skLineSegment(sketch, "E364.MirrorCS", {"start": v(-49.17, 57.63) * mm, "end": v(-49.17, 72.63) * mm});
            skLineSegment(sketch, "E365.MirrorCS", {"start": v(-52.17, 87.63) * mm, "end": v(-52.17, 80.13) * mm});
            skLineSegment(sketch, "E366.MirrorCS", {"start": v(-52.17, 42.63) * mm, "end": v(-52.17, 57.63) * mm});
            skLineSegment(sketch, "E367.MirrorCS", {"start": v(-52.17, 72.63) * mm, "end": v(-52.17, 80.13) * mm});
            skLineSegment(sketch, "E368.MirrorCS", {"start": v(-52.17, 117.63) * mm, "end": v(-52.17, 102.63) * mm});
            skLineSegment(sketch, "E369.MirrorCS", {"start": v(-49.17, 129.63) * mm, "end": v(-49.17, 117.63) * mm});
            skLineSegment(sketch, "E370", {"start": v(52.83, 80.13) * mm, "end": v(-52.17, 80.13) * mm, "construction": true});
            skLineSegment(sketch, "E371.MirrorCS", {"start": v(37.83, 30.63) * mm, "end": v(49.83, 30.63) * mm});
            skLineSegment(sketch, "E372.MirrorCS", {"start": v(-37.17, 30.63) * mm, "end": v(-49.17, 30.63) * mm});
            skLineSegment(sketch, "E373.MirrorCS", {"start": v(7.83, 30.63) * mm, "end": v(7.83, 27.63) * mm});
            skLineSegment(sketch, "E374.MirrorCS", {"start": v(-37.17, 27.63) * mm, "end": v(-37.17, 30.63) * mm});
            skLineSegment(sketch, "E375.MirrorCS", {"start": v(-22.17, 30.63) * mm, "end": v(-22.17, 27.63) * mm});
            skLineSegment(sketch, "E376.MirrorCS", {"start": v(-7.17, 27.63) * mm, "end": v(-7.17, 30.63) * mm});
            skLineSegment(sketch, "E377.MirrorCS", {"start": v(37.83, 30.63) * mm, "end": v(37.83, 27.63) * mm});
            skLineSegment(sketch, "E378.MirrorCS", {"start": v(22.83, 27.63) * mm, "end": v(22.83, 30.63) * mm});
            skLineSegment(sketch, "E379.MirrorCS", {"start": v(22.83, 30.63) * mm, "end": v(7.83, 30.63) * mm});
            skPoint(sketch, "E380.MirrorP", {"position": v(0.33, 27.63) * mm});
            skLineSegment(sketch, "E381.MirrorCS", {"start": v(37.83, 27.63) * mm, "end": v(22.83, 27.63) * mm});
            skLineSegment(sketch, "E382.MirrorCS", {"start": v(-7.17, 30.63) * mm, "end": v(-22.17, 30.63) * mm});
            skLineSegment(sketch, "E383.MirrorCS", {"start": v(7.83, 27.63) * mm, "end": v(-7.17, 27.63) * mm});
            skLineSegment(sketch, "E384.MirrorCS", {"start": v(-22.17, 27.63) * mm, "end": v(-37.17, 27.63) * mm});
            skLineSegment(sketch, "E385", {"start": v(-85.61, -186.4) * mm, "end": v(-85.61, -201.4) * mm});
            skLineSegment(sketch, "E386", {"start": v(-85.61, -201.4) * mm, "end": v(-88.61, -201.4) * mm});
            skLineSegment(sketch, "E387", {"start": v(-105.92, -201.4) * mm, "end": v(-105.92, -186.4) * mm, "construction": true});
            skLineSegment(sketch, "E388", {"start": v(-88.61, -201.4) * mm, "end": v(-88.61, -216.4) * mm});
            skLineSegment(sketch, "E389", {"start": v(-88.61, -216.4) * mm, "end": v(-85.61, -216.4) * mm});
            skLineSegment(sketch, "E390", {"start": v(-85.61, -186.4) * mm, "end": v(-92.68, -193.47) * mm, "construction": true});
            skLineSegment(sketch, "E391.MirrorCS", {"start": v(-100.61, -186.4) * mm, "end": v(-100.61, -189.4) * mm});
            skLineSegment(sketch, "E392.MirrorCS", {"start": v(-100.61, -189.4) * mm, "end": v(-115.61, -189.4) * mm});
            skLineSegment(sketch, "E393.MirrorCS", {"start": v(-115.61, -189.4) * mm, "end": v(-115.61, -186.4) * mm});
            skLineSegment(sketch, "E394.MirrorCS", {"start": v(-85.61, -186.4) * mm, "end": v(-100.61, -186.4) * mm});
            skLineSegment(sketch, "E395.1.0.0", {"start": v(-130.61, -189.4) * mm, "end": v(-145.61, -189.4) * mm});
            skLineSegment(sketch, "E395.1.0.1", {"start": v(-145.61, -189.4) * mm, "end": v(-145.61, -186.4) * mm});
            skLineSegment(sketch, "E395.1.0.2", {"start": v(-130.61, -186.4) * mm, "end": v(-130.61, -189.4) * mm});
            skLineSegment(sketch, "E395.1.0.3", {"start": v(-115.61, -186.4) * mm, "end": v(-130.61, -186.4) * mm});
            skLineSegment(sketch, "E395.2.0.0", {"start": v(-160.61, -189.4) * mm, "end": v(-175.61, -189.4) * mm});
            skLineSegment(sketch, "E395.2.0.1", {"start": v(-175.61, -189.4) * mm, "end": v(-175.61, -186.4) * mm});
            skLineSegment(sketch, "E395.2.0.2", {"start": v(-160.61, -186.4) * mm, "end": v(-160.61, -189.4) * mm});
            skLineSegment(sketch, "E395.2.0.3", {"start": v(-145.61, -186.4) * mm, "end": v(-160.61, -186.4) * mm});
            skLineSegment(sketch, "E395.direction1", {"start": v(-115.61, -189.4) * mm, "end": v(-145.61, -189.4) * mm, "construction": true});
            skLineSegment(sketch, "E396", {"start": v(-175.61, -186.4) * mm, "end": v(-190.61, -186.4) * mm});
            skLineSegment(sketch, "E397.0.1.0", {"start": v(-88.61, -231.4) * mm, "end": v(-88.61, -246.4) * mm});
            skLineSegment(sketch, "E397.0.1.1", {"start": v(-85.61, -216.4) * mm, "end": v(-85.61, -231.4) * mm});
            skLineSegment(sketch, "E397.0.1.2", {"start": v(-88.61, -246.4) * mm, "end": v(-85.61, -246.4) * mm});
            skLineSegment(sketch, "E397.0.1.3", {"start": v(-85.61, -231.4) * mm, "end": v(-88.61, -231.4) * mm});
            skLineSegment(sketch, "E397.0.2.0", {"start": v(-88.61, -261.4) * mm, "end": v(-88.61, -276.4) * mm});
            skLineSegment(sketch, "E397.0.2.1", {"start": v(-85.61, -246.4) * mm, "end": v(-85.61, -261.4) * mm});
            skLineSegment(sketch, "E397.0.2.2", {"start": v(-88.61, -276.4) * mm, "end": v(-85.61, -276.4) * mm});
            skLineSegment(sketch, "E397.0.2.3", {"start": v(-85.61, -261.4) * mm, "end": v(-88.61, -261.4) * mm});
            skLineSegment(sketch, "E397.0.3.0", {"start": v(-88.61, -291.4) * mm, "end": v(-88.61, -306.4) * mm});
            skLineSegment(sketch, "E397.0.3.1", {"start": v(-85.61, -276.4) * mm, "end": v(-85.61, -291.4) * mm});
            skLineSegment(sketch, "E397.0.3.2", {"start": v(-88.61, -306.4) * mm, "end": v(-85.61, -306.4) * mm});
            skLineSegment(sketch, "E397.0.3.3", {"start": v(-85.61, -291.4) * mm, "end": v(-88.61, -291.4) * mm});
            skLineSegment(sketch, "E397.direction1", {"start": v(-88.61, -216.4) * mm, "end": v(-63.61, -216.4) * mm, "construction": true});
            skLineSegment(sketch, "E397.direction2", {"start": v(-88.61, -216.4) * mm, "end": v(-88.61, -246.4) * mm, "construction": true});
            skLineSegment(sketch, "E398.0.0.4", {"start": v(-88.61, -321.4) * mm, "end": v(-88.61, -336.4) * mm});
            skLineSegment(sketch, "E398.3.0.4", {"start": v(-85.61, -306.4) * mm, "end": v(-85.61, -321.4) * mm});
            skLineSegment(sketch, "E398.6.0.4", {"start": v(-88.61, -336.4) * mm, "end": v(-85.61, -336.4) * mm});
            skLineSegment(sketch, "E398.9.0.4", {"start": v(-85.61, -321.4) * mm, "end": v(-88.61, -321.4) * mm});
            skLineSegment(sketch, "E399", {"start": v(-85.61, -336.4) * mm, "end": v(-85.61, -351.4) * mm});
            skLineSegment(sketch, "E400.MirrorCS", {"start": v(-187.61, -306.4) * mm, "end": v(-190.61, -306.4) * mm});
            skLineSegment(sketch, "E401.MirrorCS", {"start": v(-190.61, -201.4) * mm, "end": v(-187.61, -201.4) * mm});
            skLineSegment(sketch, "E402.MirrorCS", {"start": v(-187.61, -276.4) * mm, "end": v(-190.61, -276.4) * mm});
            skLineSegment(sketch, "E403.MirrorCS", {"start": v(-187.61, -336.4) * mm, "end": v(-190.61, -336.4) * mm});
            skLineSegment(sketch, "E404.MirrorCS", {"start": v(-187.61, -216.4) * mm, "end": v(-190.61, -216.4) * mm});
            skLineSegment(sketch, "E405.MirrorCS", {"start": v(-190.61, -231.4) * mm, "end": v(-187.61, -231.4) * mm});
            skLineSegment(sketch, "E406.MirrorCS", {"start": v(-190.61, -321.4) * mm, "end": v(-187.61, -321.4) * mm});
            skLineSegment(sketch, "E407.MirrorCS", {"start": v(-190.61, -291.4) * mm, "end": v(-187.61, -291.4) * mm});
            skLineSegment(sketch, "E408.MirrorCS", {"start": v(-190.61, -261.4) * mm, "end": v(-187.61, -261.4) * mm});
            skLineSegment(sketch, "E409.MirrorCS", {"start": v(-187.61, -246.4) * mm, "end": v(-190.61, -246.4) * mm});
            skLineSegment(sketch, "E410.MirrorCS", {"start": v(-187.61, -231.4) * mm, "end": v(-187.61, -246.4) * mm});
            skLineSegment(sketch, "E411.MirrorCS", {"start": v(-187.61, -201.4) * mm, "end": v(-187.61, -216.4) * mm});
            skLineSegment(sketch, "E412.MirrorCS", {"start": v(-187.61, -261.4) * mm, "end": v(-187.61, -276.4) * mm});
            skLineSegment(sketch, "E413.MirrorCS", {"start": v(-190.61, -216.4) * mm, "end": v(-190.61, -231.4) * mm});
            skLineSegment(sketch, "E414.MirrorCS", {"start": v(-187.61, -291.4) * mm, "end": v(-187.61, -306.4) * mm});
            skLineSegment(sketch, "E415.MirrorCS", {"start": v(-190.61, -186.4) * mm, "end": v(-190.61, -201.4) * mm});
            skLineSegment(sketch, "E416.MirrorCS", {"start": v(-190.61, -246.4) * mm, "end": v(-190.61, -261.4) * mm});
            skLineSegment(sketch, "E417.MirrorCS", {"start": v(-187.61, -321.4) * mm, "end": v(-187.61, -336.4) * mm});
            skLineSegment(sketch, "E418.MirrorCS", {"start": v(-190.61, -306.4) * mm, "end": v(-190.61, -321.4) * mm});
            skLineSegment(sketch, "E419.MirrorCS", {"start": v(-190.61, -336.4) * mm, "end": v(-190.61, -351.4) * mm});
            skLineSegment(sketch, "E420.MirrorCS", {"start": v(-190.61, -276.4) * mm, "end": v(-190.61, -291.4) * mm});
            skLineSegment(sketch, "E421", {"start": v(-88.61, -268.9) * mm, "end": v(-187.61, -268.9) * mm, "construction": true});
            skLineSegment(sketch, "E422.MirrorCS", {"start": v(-175.61, -348.4) * mm, "end": v(-175.61, -351.4) * mm});
            skLineSegment(sketch, "E423.MirrorCS", {"start": v(-130.61, -351.4) * mm, "end": v(-130.61, -348.4) * mm});
            skLineSegment(sketch, "E424.MirrorCS", {"start": v(-160.61, -351.4) * mm, "end": v(-160.61, -348.4) * mm});
            skLineSegment(sketch, "E425.MirrorCS", {"start": v(-115.61, -348.4) * mm, "end": v(-115.61, -351.4) * mm});
            skLineSegment(sketch, "E426.MirrorCS", {"start": v(-145.61, -348.4) * mm, "end": v(-145.61, -351.4) * mm});
            skLineSegment(sketch, "E427.MirrorCS", {"start": v(-100.61, -351.4) * mm, "end": v(-100.61, -348.4) * mm});
            skLineSegment(sketch, "E428.MirrorCS", {"start": v(-130.61, -348.4) * mm, "end": v(-145.61, -348.4) * mm});
            skLineSegment(sketch, "E429.MirrorCS", {"start": v(-145.61, -351.4) * mm, "end": v(-160.61, -351.4) * mm});
            skLineSegment(sketch, "E430.MirrorCS", {"start": v(-85.61, -351.4) * mm, "end": v(-100.61, -351.4) * mm});
            skLineSegment(sketch, "E431.MirrorCS", {"start": v(-100.61, -348.4) * mm, "end": v(-115.61, -348.4) * mm});
            skLineSegment(sketch, "E432.MirrorCS", {"start": v(-160.61, -348.4) * mm, "end": v(-175.61, -348.4) * mm});
            skLineSegment(sketch, "E433.MirrorCS", {"start": v(-190.61, -351.4) * mm, "end": v(-190.61, -336.4) * mm});
            skLineSegment(sketch, "E434.MirrorCS", {"start": v(-175.61, -351.4) * mm, "end": v(-190.61, -351.4) * mm});
            skLineSegment(sketch, "E435.MirrorCS", {"start": v(-115.61, -351.4) * mm, "end": v(-130.61, -351.4) * mm});
            skLineSegment(sketch, "E436", {"start": v(-297.58, -268.78) * mm, "end": v(-184.33, -268.78) * mm, "construction": true});
            skLineSegment(sketch, "E437.bottom", {"start": v(-158.92, -308.76) * mm, "end": v(-117.3, -308.76) * mm});
            skLineSegment(sketch, "E437.top", {"start": v(-158.92, -219.04) * mm, "end": v(-117.3, -219.04) * mm});
            skLineSegment(sketch, "E437.left", {"start": v(-163.92, -303.76) * mm, "end": v(-163.92, -224.04) * mm});
            skLineSegment(sketch, "E437.right", {"start": v(-112.3, -303.76) * mm, "end": v(-112.3, -224.04) * mm});
            skPoint(sketch, "E437.middle", {"position": v(-138.11, -268.9) * mm});
            skPoint(sketch, "E438.visualSharp", {"position": v(-112.3, -219.04) * mm});
            skArc(sketch, "E438.filletArc", {"start": v(-112.3, -224.04) * mm, "mid": v(-113.76, -220.5) * mm, "end": v(-117.3, -219.04) * mm});
            skPoint(sketch, "E439.visualSharp", {"position": v(-112.3, -318.76) * mm});
            skArc(sketch, "E439.filletArc", {"start": v(-117.3, -308.76) * mm, "mid": v(-113.76, -307.3) * mm, "end": v(-112.3, -303.76) * mm});
            skPoint(sketch, "E440.visualSharp", {"position": v(-163.92, -219.04) * mm});
            skArc(sketch, "E440.filletArc", {"start": v(-158.92, -219.04) * mm, "mid": v(-162.46, -220.5) * mm, "end": v(-163.92, -224.04) * mm});
            skPoint(sketch, "E441.visualSharp", {"position": v(-163.92, -318.76) * mm});
            skArc(sketch, "E441.filletArc", {"start": v(-163.92, -303.76) * mm, "mid": v(-162.46, -307.3) * mm, "end": v(-158.92, -308.76) * mm});
            skText(sketch, "E442", { "text": "The Tapper v1.0", "fontName": "OpenSans-Bold.ttf"});
            skLineSegment(sketch, "E443", {"start": v(0, -3.75) * mm, "end": v(0, -108.75) * mm, "construction": true});
            skPoint(sketch, "E443.endSnap0", {"position": v(0, -56.5) * mm});
            skCircle(sketch, "E444", {"center": v(-15, -108.75) * mm, "radius": 2.25 * mm});
            skLineSegment(sketch, "E445", {"start": v(-138.11, -348.4) * mm, "end": v(-138.11, -321.15) * mm, "construction": true});
            skCircle(sketch, "E446", {"center": v(-153.11, -321.15) * mm, "radius": 2.25 * mm});
            skLineSegment(sketch, "E447", {"start": v(136.44, -28.75) * mm, "end": v(146.44, -28.75) * mm, "construction": true});
            skArc(sketch, "E448", {"start": v(139.56, -26.25) * mm, "mid": v(138.05, -25.09) * mm, "end": v(136.17, -24.76) * mm});
            skLineSegment(sketch, "E449.0", {"start": v(139.56, -31.25) * mm, "end": v(150.44, -31.25) * mm});
            skLineSegment(sketch, "E450.0", {"start": v(139.56, -26.25) * mm, "end": v(150.44, -26.25) * mm});
            skLineSegment(sketch, "E451.0", {"start": v(140.4, -33.25) * mm, "end": v(150.44, -33.25) * mm});
            skArc(sketch, "E451.1", {"start": v(140.4, -24.25) * mm, "mid": v(138.28, -23.04) * mm, "end": v(135.84, -22.78) * mm});
            skLineSegment(sketch, "E451.2", {"start": v(140.4, -24.25) * mm, "end": v(150.44, -24.25) * mm});
            skLineSegment(sketch, "E452", {"start": v(194.14, -32.25) * mm, "end": v(194.14, -32.25) * mm});
            skLineSegment(sketch, "E453", {"start": v(194.14, -25.25) * mm, "end": v(194.14, -25.25) * mm});
            skArc(sketch, "E454.trimOffspring", {"start": v(135.84, -34.72) * mm, "mid": v(138.28, -34.46) * mm, "end": v(140.4, -33.25) * mm});
            skArc(sketch, "E455.trimOffspring", {"start": v(136.17, -32.74) * mm, "mid": v(138.05, -32.41) * mm, "end": v(139.56, -31.25) * mm});
            skArc(sketch, "E456.trimOffspring", {"start": v(135.84, -22.78) * mm, "mid": v(76.44, -28.75) * mm, "end": v(135.84, -34.72) * mm});
            skPoint(sketch, "E457.middle", {"position": v(127.12, -79.98) * mm});
            skPoint(sketch, "E458.visualSharp", {"position": v(73.7, -52.08) * mm});
            skArc(sketch, "E458.filletArc", {"start": v(74.41, -52.77) * mm, "mid": v(73.7, -52.49) * mm, "end": v(73, -52.8) * mm});
            skPoint(sketch, "E459.visualSharp", {"position": v(71.96, -53.88) * mm});
            skArc(sketch, "E459.filletArc", {"start": v(72.65, -53.16) * mm, "mid": v(72.37, -53.87) * mm, "end": v(72.68, -54.57) * mm});
            skPoint(sketch, "E460.visualSharp", {"position": v(68.5, -57.49) * mm});
            skArc(sketch, "E460.filletArc", {"start": v(69.22, -58.18) * mm, "mid": v(68.5, -57.9) * mm, "end": v(67.8, -58.21) * mm});
            skPoint(sketch, "E461.visualSharp", {"position": v(66.77, -59.3) * mm});
            skArc(sketch, "E461.filletArc", {"start": v(67.46, -58.57) * mm, "mid": v(67.18, -59.29) * mm, "end": v(67.5, -59.99) * mm});
            skPoint(sketch, "E462.visualSharp", {"position": v(151.44, -33.25) * mm});
            skArc(sketch, "E462.filletArc", {"start": v(150.44, -33.25) * mm, "mid": v(151.15, -32.96) * mm, "end": v(151.44, -32.25) * mm});
            skPoint(sketch, "E463.visualSharp", {"position": v(151.44, -31.25) * mm});
            skArc(sketch, "E463.filletArc", {"start": v(151.44, -32.25) * mm, "mid": v(151.15, -31.54) * mm, "end": v(150.44, -31.25) * mm});
            skPoint(sketch, "E464.visualSharp", {"position": v(151.44, -26.25) * mm});
            skArc(sketch, "E464.filletArc", {"start": v(150.44, -26.25) * mm, "mid": v(151.15, -25.96) * mm, "end": v(151.44, -25.25) * mm});
            skPoint(sketch, "E465.visualSharp", {"position": v(151.44, -24.25) * mm});
            skArc(sketch, "E465.filletArc", {"start": v(151.44, -25.25) * mm, "mid": v(151.15, -24.54) * mm, "end": v(150.44, -24.25) * mm});
            skPoint(sketch, "E466.1.0", {"position": v(131.57, -63.23) * mm});
            skLineSegment(sketch, "E466.1.1", {"start": v(142.17, -63) * mm, "end": v(137.67, -67.7) * mm});
            skArc(sketch, "E466.1.2", {"start": v(142.76, -62.4) * mm, "mid": v(146.52, -51.24) * mm, "end": v(135.54, -55.47) * mm});
            skLineSegment(sketch, "E466.1.3", {"start": v(140.37, -61.27) * mm, "end": v(135.87, -65.97) * mm});
            skPoint(sketch, "E466.1.4", {"position": v(135.18, -66.69) * mm});
            skLineSegment(sketch, "E466.1.5", {"start": v(136.76, -57.81) * mm, "end": v(132.26, -62.5) * mm});
            skLineSegment(sketch, "E466.1.6", {"start": v(134.95, -56.08) * mm, "end": v(130.46, -60.78) * mm});
            skPoint(sketch, "E466.1.7", {"position": v(136.98, -68.42) * mm});
            skLineSegment(sketch, "E466.1.8", {"start": v(140.22, -54.2) * mm, "end": v(143.83, -57.66) * mm, "construction": true});
            skArc(sketch, "E466.1.9", {"start": v(141.67, -59.92) * mm, "mid": v(144.8, -53.05) * mm, "end": v(138.06, -56.46) * mm});
            skArc(sketch, "E466.1.10", {"start": v(136.26, -67.73) * mm, "mid": v(136.97, -68) * mm, "end": v(137.67, -67.7) * mm});
            skLineSegment(sketch, "E466.1.11", {"start": v(136.76, -57.81) * mm, "end": v(138.06, -56.46) * mm});
            skLineSegment(sketch, "E466.1.12", {"start": v(140.37, -61.27) * mm, "end": v(141.67, -59.92) * mm});
            skLineSegment(sketch, "E466.1.13", {"start": v(135.9, -67.38) * mm, "end": v(136.26, -67.73) * mm});
            skLineSegment(sketch, "E466.1.14", {"start": v(142.17, -63) * mm, "end": v(142.76, -62.4) * mm});
            skLineSegment(sketch, "E466.1.15", {"start": v(134.95, -56.08) * mm, "end": v(135.54, -55.47) * mm});
            skArc(sketch, "E466.1.16", {"start": v(130.85, -62.54) * mm, "mid": v(131.56, -62.81) * mm, "end": v(132.26, -62.5) * mm});
            skArc(sketch, "E466.1.17", {"start": v(135.87, -65.97) * mm, "mid": v(135.6, -66.68) * mm, "end": v(135.9, -67.38) * mm});
            skArc(sketch, "E466.1.18", {"start": v(130.46, -60.78) * mm, "mid": v(130.18, -61.49) * mm, "end": v(130.49, -62.19) * mm});
            skLineSegment(sketch, "E466.1.19", {"start": v(130.85, -62.54) * mm, "end": v(130.49, -62.19) * mm});
            skPoint(sketch, "E466.2.0", {"position": v(140.92, -3.62) * mm});
            skLineSegment(sketch, "E466.2.1", {"start": v(140.7, 6.98) * mm, "end": v(145.38, 2.49) * mm});
            skArc(sketch, "E466.2.2", {"start": v(140.08, 7.57) * mm, "mid": v(128.93, 11.33) * mm, "end": v(133.16, 0.35) * mm});
            skLineSegment(sketch, "E466.2.3", {"start": v(138.96, 5.18) * mm, "end": v(143.65, 0.68) * mm});
            skPoint(sketch, "E466.2.4", {"position": v(144.38, -0.01) * mm});
            skLineSegment(sketch, "E466.2.5", {"start": v(135.5, 1.57) * mm, "end": v(140.2, -2.93) * mm});
            skLineSegment(sketch, "E466.2.6", {"start": v(133.77, -0.23) * mm, "end": v(138.46, -4.73) * mm});
            skPoint(sketch, "E466.2.7", {"position": v(146.1, 1.8) * mm});
            skLineSegment(sketch, "E466.2.8", {"start": v(131.9, 5.03) * mm, "end": v(135.35, 8.64) * mm, "construction": true});
            skArc(sketch, "E466.2.9", {"start": v(137.6, 6.48) * mm, "mid": v(130.73, 9.6) * mm, "end": v(134.15, 2.87) * mm});
            skArc(sketch, "E466.2.10", {"start": v(145.41, 1.07) * mm, "mid": v(145.7, 1.79) * mm, "end": v(145.38, 2.49) * mm});
            skLineSegment(sketch, "E466.2.11", {"start": v(135.5, 1.57) * mm, "end": v(134.15, 2.87) * mm});
            skLineSegment(sketch, "E466.2.12", {"start": v(138.96, 5.18) * mm, "end": v(137.6, 6.48) * mm});
            skLineSegment(sketch, "E466.2.13", {"start": v(145.07, 0.71) * mm, "end": v(145.41, 1.07) * mm});
            skLineSegment(sketch, "E466.2.14", {"start": v(140.7, 6.98) * mm, "end": v(140.08, 7.57) * mm});
            skLineSegment(sketch, "E466.2.15", {"start": v(133.77, -0.23) * mm, "end": v(133.16, 0.35) * mm});
            skArc(sketch, "E466.2.16", {"start": v(140.22, -4.34) * mm, "mid": v(140.5, -3.63) * mm, "end": v(140.2, -2.93) * mm});
            skArc(sketch, "E466.2.17", {"start": v(143.65, 0.68) * mm, "mid": v(144.37, 0.4) * mm, "end": v(145.07, 0.71) * mm});
            skArc(sketch, "E466.2.18", {"start": v(138.46, -4.73) * mm, "mid": v(139.18, -5.01) * mm, "end": v(139.88, -4.7) * mm});
            skLineSegment(sketch, "E466.2.19", {"start": v(140.22, -4.34) * mm, "end": v(139.88, -4.7) * mm});
            skPoint(sketch, "E466.3.0", {"position": v(81.3, 5.73) * mm});
            skLineSegment(sketch, "E466.3.1", {"start": v(70.7, 5.5) * mm, "end": v(75.2, 10.2) * mm});
            skArc(sketch, "E466.3.2", {"start": v(70.12, 4.9) * mm, "mid": v(66.36, -6.26) * mm, "end": v(77.34, -2.03) * mm});
            skLineSegment(sketch, "E466.3.3", {"start": v(72.5, 3.77) * mm, "end": v(77, 8.47) * mm});
            skPoint(sketch, "E466.3.4", {"position": v(77.7, 9.19) * mm});
            skLineSegment(sketch, "E466.3.5", {"start": v(76.12, 0.31) * mm, "end": v(80.62, 5) * mm});
            skLineSegment(sketch, "E466.3.6", {"start": v(77.92, -1.42) * mm, "end": v(82.42, 3.28) * mm});
            skPoint(sketch, "E466.3.7", {"position": v(75.9, 10.92) * mm});
            skLineSegment(sketch, "E466.3.8", {"start": v(72.66, -3.3) * mm, "end": v(69.05, 0.16) * mm, "construction": true});
            skArc(sketch, "E466.3.9", {"start": v(71.2, 2.42) * mm, "mid": v(68.09, -4.45) * mm, "end": v(74.82, -1.04) * mm});
            skArc(sketch, "E466.3.10", {"start": v(76.62, 10.23) * mm, "mid": v(75.9, 10.5) * mm, "end": v(75.2, 10.2) * mm});
            skLineSegment(sketch, "E466.3.11", {"start": v(76.12, 0.31) * mm, "end": v(74.82, -1.04) * mm});
            skLineSegment(sketch, "E466.3.12", {"start": v(72.5, 3.77) * mm, "end": v(71.2, 2.42) * mm});
            skLineSegment(sketch, "E466.3.13", {"start": v(76.98, 9.88) * mm, "end": v(76.62, 10.23) * mm});
            skLineSegment(sketch, "E466.3.14", {"start": v(70.7, 5.5) * mm, "end": v(70.12, 4.9) * mm});
            skLineSegment(sketch, "E466.3.15", {"start": v(77.92, -1.42) * mm, "end": v(77.34, -2.03) * mm});
            skArc(sketch, "E466.3.16", {"start": v(82.03, 5.04) * mm, "mid": v(81.32, 5.31) * mm, "end": v(80.62, 5) * mm});
            skArc(sketch, "E466.3.17", {"start": v(77, 8.47) * mm, "mid": v(77.28, 9.18) * mm, "end": v(76.98, 9.88) * mm});
            skArc(sketch, "E466.3.18", {"start": v(82.42, 3.28) * mm, "mid": v(82.7, 3.99) * mm, "end": v(82.4, 4.69) * mm});
            skLineSegment(sketch, "E466.3.19", {"start": v(82.03, 5.04) * mm, "end": v(82.4, 4.69) * mm});
            skLineSegment(sketch, "E467", {"start": v(0, -108.75) * mm, "end": v(-15, -108.75) * mm, "construction": true});
            skLineSegment(sketch, "E468", {"start": v(-138.11, -321.15) * mm, "end": v(-153.11, -321.15) * mm, "construction": true});
            skCircle(sketch, "E469", {"center": v(-36.15, -56.5) * mm, "radius": 3.25 * mm});
            skCircle(sketch, "E470", {"center": v(106.44, -115.4) * mm, "radius": 3.25 * mm});
            skLineSegment(sketch, "E471.bottom", {"start": v(241.5, 155.5) * mm, "end": v(-58.5, 155.5) * mm});
            skLineSegment(sketch, "E471.top", {"start": v(241.5, -144.5) * mm, "end": v(-58.5, -144.5) * mm});
            skLineSegment(sketch, "E471.left", {"start": v(241.5, 155.5) * mm, "end": v(241.5, -144.5) * mm});
            skLineSegment(sketch, "E471.right", {"start": v(-58.5, 155.5) * mm, "end": v(-58.5, -144.5) * mm, "construction": true});
            const initialGuessF5  = {"E442": [-0.10706, -0.2289, 0, -1, 0.00732]};
            skSetInitialGuess(sketch, initialGuessF5);
            skSolve(sketch);
        }
        {
            var Q0;
            Q0=makeQuery(id+"F5.imprint","IMPRINT",FACE,{"disambiguationData":[TD([[makeQuery(id+"F5.imprint","IMPRINT",EDGE,{"derivedFrom":sQuery(id+"F5.wireOp",EDGE,"bf0e35a7-cca4-4cab-8c9f-da47d86e69d5.0")}),-1.0]])]});
            var Q1;
            Q1=makeQuery(id+"F5.imprint","IMPRINT",FACE,{"disambiguationData":[TD([[makeQuery(id+"F5.imprint","IMPRINT",EDGE,{"derivedFrom":sQuery(id+"F5.wireOp",EDGE,"c2f81db9-d668-4b26-950f-16d0a29487280.MirrorCS")}),-1.0]])]});
            var Q2;
            Q2=makeQuery(id+"F5.imprint","IMPRINT",FACE,{"disambiguationData":[TD([[makeQuery(id+"F5.imprint","IMPRINT",EDGE,{"derivedFrom":sQuery(id+"F5.wireOp",EDGE,"386f4eb1-01be-45ac-a4d4-7880b8e78a1f.1")}),-1.0]])]});
            var Q3;
            Q3=makeQuery(id+"F5.imprint","IMPRINT",FACE,{"disambiguationData":[TD([[makeQuery(id+"F5.imprint","IMPRINT",EDGE,{"derivedFrom":sQuery(id+"F5.wireOp",EDGE,"386f4eb1-01be-45ac-a4d4-7880b8e78a1f.0")}),1.0]])]});
            var Q4;
            {var subQ0=sQuery(id+"F5.wireOp",EDGE,"E14");Q4=makeQuery(id+"F5.imprint","IMPRINT",FACE,{"disambiguationData":[TD([[makeQuery(id+"F5.imprint","IMPRINT",EDGE,{"derivedFrom":subQ0}),-1.0]])]});}
            var Q5;
            {var subQ0=sQuery(id+"F5.wireOp",EDGE,"E18");Q5=makeQuery(id+"F5.imprint","IMPRINT",FACE,{"disambiguationData":[TD([[makeQuery(id+"F5.imprint","IMPRINT",EDGE,{"derivedFrom":subQ0}),-1.0]])]});}
            var Q6;
            {var subQ0=sQuery(id+"F5.wireOp",EDGE,"E16");Q6=makeQuery(id+"F5.imprint","IMPRINT",FACE,{"disambiguationData":[TD([[makeQuery(id+"F5.imprint","IMPRINT",EDGE,{"derivedFrom":subQ0}),-1.0]])]});}
            var Q7;
            {var subQ1=sQuery(id+"F5.wireOp",EDGE,"E16");Q7=makeQuery(id+"F5.imprint","IMPRINT",FACE,{"disambiguationData":[TD([[makeQuery(id+"F5.imprint","IMPRINT",EDGE,{"derivedFrom":subQ1}),1.0]])]});}
            var Q8;
            {var subQ0=sQuery(id+"F5.wireOp",EDGE,"idc2G8VQ-x4qj-ruDv-MnRS-LHltTA14USuG");Q8=makeQuery(id+"F5.imprint","IMPRINT",FACE,{"disambiguationData":[TD([[makeQuery(id+"F5.imprint","IMPRINT",EDGE,{"derivedFrom":subQ0}),-1.0]])]});}
            var Q9;
            {var subQ8=sQuery(id+"F5.wireOp",EDGE,"e864a5e8-5cc1-4ade-a80b-b134ff53a9b91.MirrorCS");Q9=makeQuery(id+"F5.imprint","IMPRINT",FACE,{"disambiguationData":[TD([[makeQuery(id+"F5.imprint","IMPRINT",EDGE,{"derivedFrom":subQ8}),1.0]])]});}
            var Q10;
            {var subQ0=sQuery(id+"F5.wireOp",EDGE,"e05a48c2-92e9-4173-95fd-20d618be50cd1.MirrorCS");Q10=makeQuery(id+"F5.imprint","IMPRINT",FACE,{"disambiguationData":[TD([[makeQuery(id+"F5.imprint","IMPRINT",EDGE,{"derivedFrom":subQ0}),-1.0]])]});}
            var Q11;
            {var subQ1=sQuery(id+"F5.wireOp",EDGE,"E19");Q11=makeQuery(id+"F5.imprint","IMPRINT",FACE,{"disambiguationData":[TD([[makeQuery(id+"F5.imprint","IMPRINT",EDGE,{"derivedFrom":subQ1}),-1.0]])]});}
            var Q12;
            {var subQ8=sQuery(id+"F5.wireOp",EDGE,"e05a48c2-92e9-4173-95fd-20d618be50cd2.MirrorCS");Q12=makeQuery(id+"F5.imprint","IMPRINT",FACE,{"disambiguationData":[TD([[makeQuery(id+"F5.imprint","IMPRINT",EDGE,{"derivedFrom":subQ8}),1.0]])]});}
            var Q13;
            {var subQ1=sQuery(id+"F5.wireOp",EDGE,"e05a48c2-92e9-4173-95fd-20d618be50cd5.MirrorCS");var subQ3=sQuery(id+"F5.wireOp",EDGE,"e05a48c2-92e9-4173-95fd-20d618be50cd8.MirrorCS");var subQ4=makeQuery(id+"F5.imprint","INTERSECT",VERTEX,{"derivedFrom":[subQ1,subQ3]});Q13=makeQuery(id+"F5.imprint","IMPRINT",FACE,{"disambiguationData":[TD([[makeQuery(id+"F5.imprint","IMPRINT",EDGE,{"disambiguationData":[TD([[subQ4,1.0]])],"derivedFrom":subQ1}),1.0]])]});}
            var Q14;
            {var subQ1=sQuery(id+"F5.wireOp",EDGE,"E20");var subQ3=sQuery(id+"F5.wireOp",EDGE,"ajGratTK-vwH1-W8cH-pOwj-Jw8JLqme7h10");var subQ4=makeQuery(id+"F5.imprint","INTERSECT",VERTEX,{"derivedFrom":[subQ1,subQ3]});Q14=makeQuery(id+"F5.imprint","IMPRINT",FACE,{"disambiguationData":[TD([[makeQuery(id+"F5.imprint","IMPRINT",EDGE,{"disambiguationData":[TD([[subQ4,1.0]])],"derivedFrom":subQ1}),-1.0]])]});}
            var Q15;
            {var subQ0=sQuery(id+"F5.wireOp",EDGE,"E23.0");var subQ1=sQuery(id+"F5.wireOp",EDGE,"e864a5e8-5cc1-4ade-a80b-b134ff53a9b92.MirrorCS");var subQ2=makeQuery(id+"F5.imprint","INTERSECT",VERTEX,{"derivedFrom":[subQ1,subQ0]});Q15=makeQuery(id+"F5.imprint","IMPRINT",FACE,{"disambiguationData":[TD([[makeQuery(id+"F5.imprint","IMPRINT",EDGE,{"disambiguationData":[TD([[subQ2,-1.0]])],"derivedFrom":subQ1}),1.0]])]});}
            var Q16;
            {var subQ0=sQuery(id+"F5.wireOp",EDGE,"E22.0");var subQ1=sQuery(id+"F5.wireOp",EDGE,"e05a48c2-92e9-4173-95fd-20d618be50cd0.MirrorCS");var subQ2=makeQuery(id+"F5.imprint","INTERSECT",VERTEX,{"derivedFrom":[subQ1,subQ0]});Q16=makeQuery(id+"F5.imprint","IMPRINT",FACE,{"disambiguationData":[TD([[makeQuery(id+"F5.imprint","IMPRINT",EDGE,{"disambiguationData":[TD([[subQ2,-1.0]])],"derivedFrom":subQ1}),-1.0]])]});}
            var Q17;
            Q17=makeQuery(id+"F5.imprint","IMPRINT",FACE,{"disambiguationData":[TD([[makeQuery(id+"F5.imprint","IMPRINT",EDGE,{"derivedFrom":sQuery(id+"F5.wireOp",EDGE,"E328.MirrorCS")}),1.0]])]});
            var Q18;
            Q18=makeQuery(id+"F5.imprint","IMPRINT",FACE,{"disambiguationData":[TD([[makeQuery(id+"F5.imprint","IMPRINT",EDGE,{"derivedFrom":sQuery(id+"F5.wireOp",EDGE,"E121.MirrorCS")}),1.0]])]});
            var Q19;
            Q19=makeQuery(id+"F5.imprint","IMPRINT",FACE,{"disambiguationData":[TD([[makeQuery(id+"F5.imprint","IMPRINT",EDGE,{"derivedFrom":sQuery(id+"F5.wireOp",EDGE,"E263.MirrorCS")}),1.0]])]});
            var Q20;
            Q20=makeQuery(id+"F5.imprint","IMPRINT",FACE,{"disambiguationData":[TD([[makeQuery(id+"F5.imprint","IMPRINT",EDGE,{"derivedFrom":sQuery(id+"F5.wireOp",EDGE,"E105.MirrorCS")}),1.0]])]});
            var Q21;
            Q21=makeQuery(id+"F5.imprint","IMPRINT",FACE,{"disambiguationData":[TD([[makeQuery(id+"F5.imprint","IMPRINT",EDGE,{"derivedFrom":sQuery(id+"F5.wireOp",EDGE,"E385")}),-1.0]])]});
            extrude(context, id + "F6", {"entities" : qUnion([Q0, Q1, Q2, Q3, Q4, Q5, Q6, Q7, Q8, Q9, Q10, Q11, Q12, Q13, Q14, Q15, Q16, Q17, Q18, Q19, Q20, Q21]), "operationType" : NewBodyOperationType.ADD, "oppositeDirection" : true, "depth" : (getVariable(context, 'woodTh')) * mm, "offsetDistance" : 25 * mm});
        }
        {
            var Q0;
            Q0=makeQuery(id+"F2.imprint","IMPRINT",FACE,{"disambiguationData":[TD([[makeQuery(id+"F2.imprint","IMPRINT",EDGE,{"derivedFrom":sQuery(id+"F2.wireOp",EDGE,"E13")}),1.0]])]});
            extrude(context, id + "F7", {"entities" : qUnion([Q0]), "depth" : 7 * mm, "offsetDistance" : 25 * mm});
        }
    });
